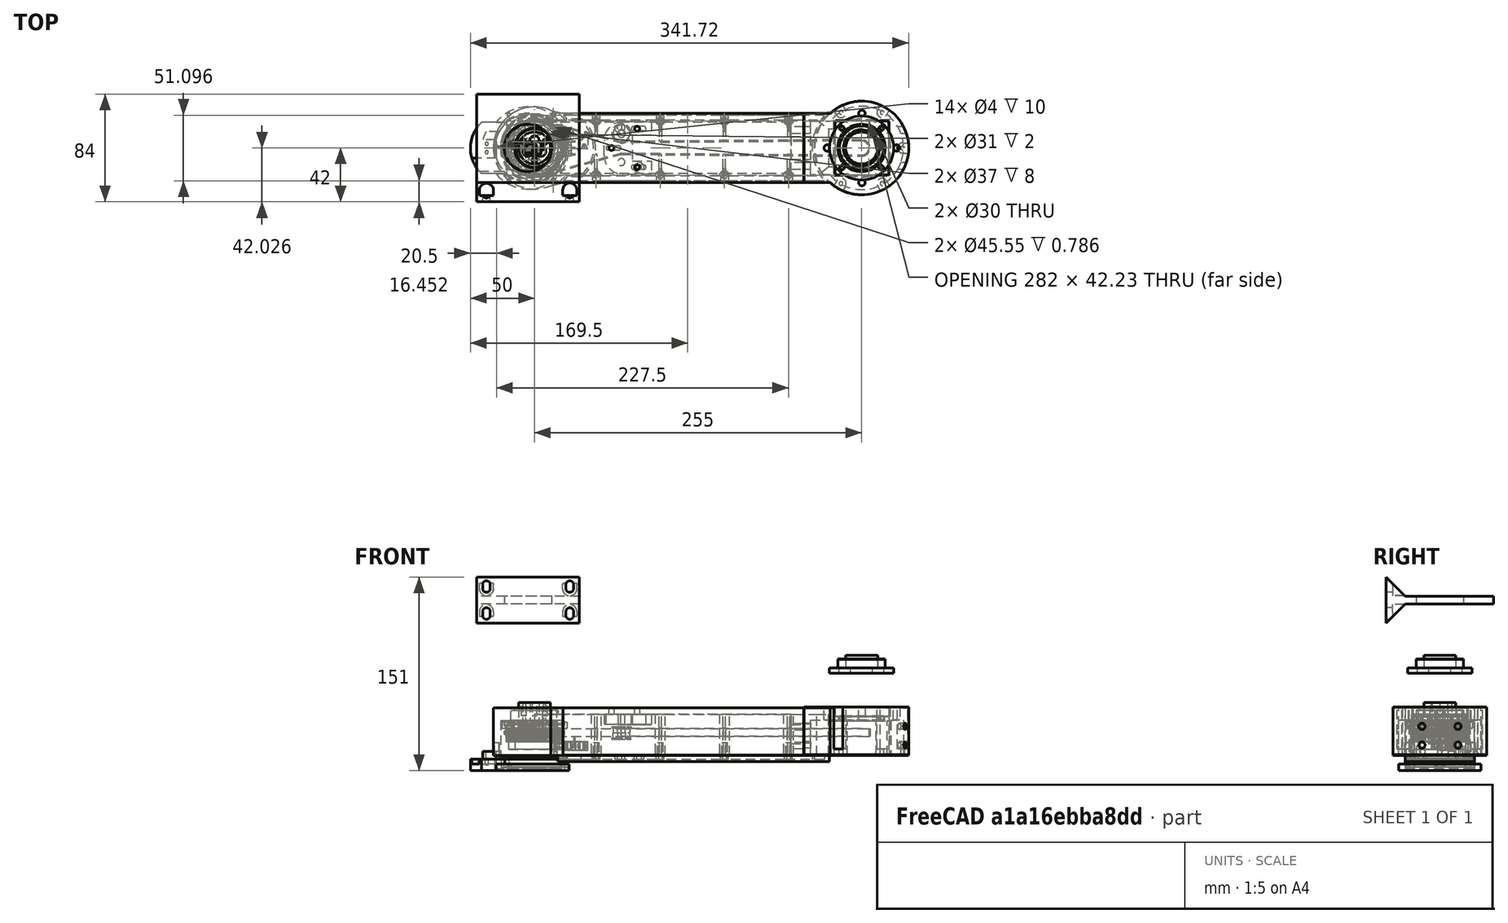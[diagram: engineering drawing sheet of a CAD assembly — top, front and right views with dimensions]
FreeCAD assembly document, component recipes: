
FREECAD ASSEMBLY — COMPONENT RECIPES ("GT2_80")

This assembly document has 18 components, labeled P0..P17 below (a component is one placed body or linked part). 13 of them carry a construction recipe — the FreeCAD feature program that regenerates the part from scratch, quoted from this document or its linked companion documents; the rest are supplied as boundary geometry only. No exploded tour is included for this assembly.
NOTE — this tour is split across 2 documents so each fits a 32k-token context. This is document 1: the component sections continue in the remaining 1 document, each repeating the header above.
COMPONENT P0 — recipe-attached ("Bearing6805-2RS", modeled in this document).
Construction recipe (the document's own serialized feature program — sketch geometry with constraints, then the solid features built on it; lengths are millimeters unless a unit is written):

FEATURE [Sketcher::SketchObject] Sketch032
  ArcFitTolerance = 0
  AttachmentSupport = -> [YZ_Plane007]
  FullyConstrained = false
  MakeInternals = false
  MapMode = 5
  Placement = pos=(0,0,0) rot=(0.57735,0.57735,0.57735;2.0944rad)
  expr: Constraints[16] = <<Spreadsheet>>.TopBearingHole / 2
  expr: Constraints[17] = <<Spreadsheet>>.TopBearingDiameter / 2
  sketch-geometry (12):
    g0: LineSegment StartX=12.5 StartY=3.5 StartZ=0 EndX=12.5 EndY=-3.5 EndZ=0
    g1: LineSegment StartX=12.5 StartY=3.5 StartZ=0 EndX=13.75 EndY=3.5 EndZ=0
    g2: LineSegment StartX=13.75 StartY=3.5 StartZ=0 EndX=14 EndY=3.25 EndZ=0
    g3: LineSegment StartX=14 StartY=3.25 StartZ=0 EndX=17.25 EndY=3.25 EndZ=0
    g4: LineSegment StartX=17.25 StartY=3.25 StartZ=0 EndX=17.5 EndY=3.5 EndZ=0
    g5: LineSegment StartX=17.5 StartY=3.5 StartZ=0 EndX=18.5 EndY=3.5 EndZ=0
    g6: LineSegment StartX=18.5 StartY=3.5 StartZ=0 EndX=18.5 EndY=-3.5 EndZ=0
    g7: LineSegment StartX=12.5 StartY=-3.5 StartZ=0 EndX=13.75 EndY=-3.5 EndZ=0
    g8: LineSegment StartX=13.75 StartY=-3.5 StartZ=0 EndX=14.6017 EndY=-3.46349 EndZ=0
    g9: LineSegment StartX=14.6017 StartY=-3.46349 StartZ=0 EndX=17.8517 EndY=-3.46349 EndZ=0
    g10: LineSegment StartX=17.8517 StartY=-3.46349 StartZ=0 EndX=17.5 EndY=-3.5 EndZ=0
    g11: LineSegment StartX=17.5 StartY=-3.5 StartZ=0 EndX=18.5 EndY=-3.5 EndZ=0
  constraints (34):
    c: Symmetric(g0,g0,g-1)
    c: DistanceY(g0,g0) = 7
    c: Coincident(g1,g0)
    c: Horizontal(g1)
    c: Coincident(g2,g1)
    c: Coincident(g3,g2)
    c: Horizontal(g3)
    c: Coincident(g4,g3)
    c: Coincident(g5,g4)
    c: Horizontal(g5)
    c: Coincident(g6,g5)
    c: Vertical(g6)
    c: Angle(g1,g2) = 2.35619
    c: DistanceY(g3,g5) = 0.25
    c: Horizontal(g4,g1)
    c: Equal(g4,g2)
    c: DistanceX(g-1,g0) = 12.5
    c: DistanceX(g-1,g6) = 18.5
    c: DistanceX(g1,g1) = 1.25
    c: DistanceX(g5,g5) = 1
    c: Equal(g0,g6)
    c: Coincident(g7,g0)
    c: Horizontal(g7)
    c: Equal(g1,g7)
    c: Coincident(g8,g7)
    c: Coincident(g9,g8)
    c: Horizontal(g9)
    c: Coincident(g10,g9)
    c: Coincident(g11,g10)
    c: Coincident(g11,g6)
    c: Horizontal(g11)
    c: Equal(g5,g11)
    c: Equal(g10,g4)
    c: Equal(g3,g9)
FEATURE [PartDesign::Revolution] Revolution
  Angle = 360
  Angle2 = 60
  Axis = (0,0,1)
  Base = (0,0,0)
  Placement = pos=(0,0,0) rot=(1,1,1;2.0944rad)
  Profile = -> Sketch032
  ReferenceAxis = -> Sketch032 [V_Axis]
  Reversed = true
  Suppressed = false
  Type = 0
FEATURE [PartDesign::Chamfer] Chamfer
  Angle = 45
  Base = -> Revolution [Edge11,Edge1,Edge10,Edge2]
  BaseFeature = -> Revolution
  ChamferType = 0
  FlipDirection = false
  Placement = pos=(0,0,0) rot=(1,1,1;2.0944rad)
  Size = 0.25
  Size2 = 1
  SupportTransform = false
  Suppressed = false
  UseAllEdges = false
FEATURE [PartDesign::Body] Body001  label="Bearing6805-2RS"
  AllowCompound = false
  Group = -> [Sketch032,Revolution,Chamfer]
  Origin = -> Origin007
  Placement = pos=(260,4e-16,56.4622) rot=(0,0,1;0rad)
  Tip = -> Chamfer
COMPONENT P1 — recipe-attached ("MainShaft", modeled in this document).
Construction recipe (the document's own serialized feature program — sketch geometry with constraints, then the solid features built on it; lengths are millimeters unless a unit is written):

FEATURE [Sketcher::SketchObject] Sketch
  ArcFitTolerance = 1e-06
  AttachmentSupport = -> [XZ_Plane008]
  FullyConstrained = true
  MakeInternals = false
  MapMode = 5
  Placement = pos=(0,0,0) rot=(1,0,0;1.5708rad)
  expr: Constraints[16] = <<Spreadsheet>>.TopBearingHole / 2
  expr: Constraints[17] = <<Spreadsheet>>.SecondShaftThroughHole / 2
  expr: Constraints[18] = <<Spreadsheet>>.TopThrustBearingDiameter / 2
  expr: Constraints[19] = <<Spreadsheet>>.TopThrustBearingDiameter / 2 + 2
  expr: Constraints[22] = <<Spreadsheet>>.TopThickness + <<Spreadsheet>>.TopBearingHeight + <<Spreadsheet>>.TopThrustBearingHeight + 5
  sketch-geometry (8):
    g0: LineSegment StartX=12.5 StartY=19 StartZ=0 EndX=12.5 EndY=1 EndZ=0
    g1: LineSegment StartX=12.5 StartY=1 StartZ=0 EndX=23.5 EndY=1 EndZ=0
    g2: LineSegment StartX=23.5 StartY=1 StartZ=0 EndX=23.5 EndY=4 EndZ=0
    g3: LineSegment StartX=23.5 StartY=4 StartZ=0 EndX=25.5 EndY=4 EndZ=0
    g4: LineSegment StartX=25.5 StartY=4 StartZ=0 EndX=25.5 EndY=-1 EndZ=0
    g5: LineSegment StartX=25.5 StartY=-1 StartZ=0 EndX=4 EndY=-1 EndZ=0
    g6: LineSegment StartX=4 StartY=-1 StartZ=0 EndX=4 EndY=19 EndZ=0
    g7: LineSegment StartX=4 StartY=19 StartZ=0 EndX=12.5 EndY=19 EndZ=0
  constraints (24):
    c: Coincident(g0,g1)
    c: Horizontal(g1)
    c: Coincident(g1,g2)
    c: Vertical(g2)
    c: Coincident(g2,g3)
    c: Horizontal(g3)
    c: Coincident(g3,g4)
    c: Vertical(g4)
    c: Coincident(g4,g5)
    c: Horizontal(g5)
    c: Coincident(g5,g6)
    c: Vertical(g6)
    c: Coincident(g6,g7)
    c: Coincident(g7,g0)
    c: Horizontal(g7)
    c: Vertical(g0,g0)
    c: Distance(g-2,g0) = 12.5
    c: Distance(g-2,g6) = 4
    c: Distance(g-2,g2) = 23.5
    c: Distance(g-2,g4) = 25.5
    c: Distance(g-1,g1) = 1
    c: Distance(g2,g2) = 3
    c: Distance(g-1,g7) = 19
    c: Distance(g-1,g5) = 1
FEATURE [PartDesign::Revolution] Revolution001
  Angle = 360
  Angle2 = 60
  Axis = (0,2e-16,1)
  Base = (0,0,0)
  Midplane = true
  Placement = pos=(0,0,0) rot=(1,0,0;1.5708rad)
  Profile = -> Sketch
  ReferenceAxis = -> Sketch [V_Axis]
  Refine = true
  Suppressed = false
  Type = 0
FEATURE [Sketcher::SketchObject] SketchGear
  ArcFitTolerance = 1e-06
  AttachmentSupport = -> [Revolution001]
  FullyConstrained = false
  MakeInternals = false
  MapMode = 5
  Placement = pos=(0,-2e-16,-1) rot=(1,0,0;3.14159rad)
  expr: Constraints[0] = <<Spreadsheet>>.SecondShaftThroughHole
  sketch-geometry (421):
    g0: ArcOfCircle CenterX=21.8777 CenterY=-0.75 CenterZ=0 NormalX=0 NormalY=0 NormalZ=1 AngleXU=7e-16 Radius=0.15 StartAngle=0 EndAngle=1.5708
    g1: ArcOfCircle CenterX=22.2237 CenterY=0.82798 CenterZ=0 NormalX=0 NormalY=0 NormalZ=-1 AngleXU=-1.3331 Radius=1.46929 StartAngle=0 EndAngle=0.255762
    g2: ArcOfCircle CenterX=21.8371 CenterY=0 CenterZ=0 NormalX=0 NormalY=0 NormalZ=-1 AngleXU=-0.984764 Radius=0.559359 StartAngle=0 EndAngle=1.96953
    g3: ArcOfCircle CenterX=22.2237 CenterY=-0.82798 CenterZ=0 NormalX=0 NormalY=0 NormalZ=-1 AngleXU=1.07734 Radius=1.46929 StartAngle=0 EndAngle=0.255762
    g4: ArcOfCircle CenterX=21.8777 CenterY=0.75 CenterZ=0 NormalX=0 NormalY=0 NormalZ=1 AngleXU=-1.5708 Radius=0.15 StartAngle=0 EndAngle=1.5708
    g5: LineSegment StartX=22.0277 StartY=0.75 StartZ=0 EndX=22.0062 EndY=1.22757 EndZ=0
    g6: ArcOfCircle CenterX=21.8568 CenterY=1.21412 CenterZ=0 NormalX=0 NormalY=0 NormalZ=1 AngleXU=0.0897598 Radius=0.15 StartAngle=0 EndAngle=1.5708
    g7: ArcOfCircle CenterX=22.06 CenterY=2.81676 CenterZ=0 NormalX=0 NormalY=0 NormalZ=-1 AngleXU=-1.42286 Radius=1.46929 StartAngle=0 EndAngle=0.255762
    g8: ArcOfCircle CenterX=21.7491 CenterY=1.95746 CenterZ=0 NormalX=0 NormalY=0 NormalZ=-1 AngleXU=-1.07452 Radius=0.559359 StartAngle=0 EndAngle=1.96953
    g9: ArcOfCircle CenterX=22.2084 CenterY=1.16747 CenterZ=0 NormalX=0 NormalY=0 NormalZ=-1 AngleXU=0.987578 Radius=1.46929 StartAngle=0 EndAngle=0.255762
    g10: ArcOfCircle CenterX=21.7224 CenterY=2.70808 CenterZ=0 NormalX=0 NormalY=0 NormalZ=1 AngleXU=-1.48104 Radius=0.15 StartAngle=0 EndAngle=1.5708
    g11: LineSegment StartX=21.8718 StartY=2.72153 StartZ=0 EndX=21.8076 EndY=3.19525 EndZ=0
    g12: ArcOfCircle CenterX=21.66 CenterY=3.16847 CenterZ=0 NormalX=0 NormalY=0 NormalZ=1 AngleXU=0.17952 Radius=0.15 StartAngle=0 EndAngle=1.5708
    g13: ArcOfCircle CenterX=21.7187 CenterY=4.78286 CenterZ=0 NormalX=0 NormalY=0 NormalZ=-1 AngleXU=-1.51262 Radius=1.46929 StartAngle=0 EndAngle=0.255762
    g14: ArcOfCircle CenterX=21.4861 CenterY=3.89916 CenterZ=0 NormalX=0 NormalY=0 NormalZ=-1 AngleXU=-1.16428 Radius=0.559359 StartAngle=0 EndAngle=1.96953
    g15: ArcOfCircle CenterX=22.0144 CenterY=3.15351 CenterZ=0 NormalX=0 NormalY=0 NormalZ=-1 AngleXU=0.897818 Radius=1.46929 StartAngle=0 EndAngle=0.255762
    g16: ArcOfCircle CenterX=21.3922 CenterY=4.64436 CenterZ=0 NormalX=0 NormalY=0 NormalZ=1 AngleXU=-1.39128 Radius=0.15 StartAngle=0 EndAngle=1.5708
    g17: LineSegment StartX=21.5398 StartY=4.67114 StartZ=0 EndX=21.4334 EndY=5.13721 EndZ=0
    g18: ArcOfCircle CenterX=21.2888 CenterY=5.0973 CenterZ=0 NormalX=0 NormalY=0 NormalZ=1 AngleXU=0.269279 Radius=0.15 StartAngle=0 EndAngle=1.5708
    g19: ArcOfCircle CenterX=21.2025 CenterY=6.71045 CenterZ=0 NormalX=0 NormalY=0 NormalZ=-1 AngleXU=-1.60238 Radius=1.46929 StartAngle=0 EndAngle=0.255762
    g20: ArcOfCircle CenterX=21.0501 CenterY=5.80946 CenterZ=0 NormalX=0 NormalY=0 NormalZ=-1 AngleXU=-1.25404 Radius=0.559359 StartAngle=0 EndAngle=1.96953
    g21: ArcOfCircle CenterX=21.6431 CenterY=5.11417 CenterZ=0 NormalX=0 NormalY=0 NormalZ=-1 AngleXU=0.808058 Radius=1.46929 StartAngle=0 EndAngle=0.255762
    g22: ArcOfCircle CenterX=20.8898 CenterY=6.54324 CenterZ=0 NormalX=0 NormalY=0 NormalZ=1 AngleXU=-1.30152 Radius=0.15 StartAngle=0 EndAngle=1.5708
    g23: LineSegment StartX=21.0343 StartY=6.58315 StartZ=0 EndX=20.8866 EndY=7.0378 EndZ=0
    g24: ArcOfCircle CenterX=20.7462 CenterY=6.98509 CenterZ=0 NormalX=0 NormalY=0 NormalZ=1 AngleXU=0.359039 Radius=0.15 StartAngle=0 EndAngle=1.5708
    g25: ArcOfCircle CenterX=20.5156 CenterY=8.58402 CenterZ=0 NormalX=0 NormalY=0 NormalZ=-1 AngleXU=-1.69214 Radius=1.46929 StartAngle=0 EndAngle=0.255762
    g26: ArcOfCircle CenterX=20.4446 CenterY=7.67299 CenterZ=0 NormalX=0 NormalY=0 NormalZ=-1 AngleXU=-1.3438 Radius=0.559359 StartAngle=0 EndAngle=1.96953
    g27: ArcOfCircle CenterX=21.0975 CenterY=7.03365 CenterZ=0 NormalX=0 NormalY=0 NormalZ=-1 AngleXU=0.718298 Radius=1.46929 StartAngle=0 EndAngle=0.255762
    g28: ArcOfCircle CenterX=20.2191 CenterY=8.38945 CenterZ=0 NormalX=0 NormalY=0 NormalZ=1 AngleXU=-1.21176 Radius=0.15 StartAngle=0 EndAngle=1.5708
    g29: LineSegment StartX=20.3596 StartY=8.44215 StartZ=0 EndX=20.1717 EndY=8.88173 EndZ=0
    g30: ArcOfCircle CenterX=20.0365 CenterY=8.81665 CenterZ=0 NormalX=0 NormalY=0 NormalZ=1 AngleXU=0.448799 Radius=0.15 StartAngle=0 EndAngle=1.5708
    g31: ArcOfCircle CenterX=19.6636 CenterY=10.3885 CenterZ=0 NormalX=0 NormalY=0 NormalZ=-1 AngleXU=-1.7819 Radius=1.46929 StartAngle=0 EndAngle=0.255762
    g32: ArcOfCircle CenterX=19.6745 CenterY=9.47474 CenterZ=0 NormalX=0 NormalY=0 NormalZ=-1 AngleXU=-1.43356 Radius=0.559359 StartAngle=0 EndAngle=1.96953
    g33: ArcOfCircle CenterX=20.3821 CenterY=8.8965 CenterZ=0 NormalX=0 NormalY=0 NormalZ=-1 AngleXU=0.628539 Radius=1.46929 StartAngle=0 EndAngle=0.255762
    g34: ArcOfCircle CenterX=19.3857 CenterY=10.1681 CenterZ=0 NormalX=0 NormalY=0 NormalZ=1 AngleXU=-1.122 Radius=0.15 StartAngle=0 EndAngle=1.5708
    g35: LineSegment StartX=19.5209 StartY=10.2332 StartZ=0 EndX=19.2943 EndY=10.6542 EndZ=0
    g36: ArcOfCircle CenterX=19.1656 CenterY=10.5772 CenterZ=0 NormalX=0 NormalY=0 NormalZ=1 AngleXU=0.538559 Radius=0.15 StartAngle=0 EndAngle=1.5708
    g37: ArcOfCircle CenterX=18.6532 CenterY=12.1093 CenterZ=0 NormalX=0 NormalY=0 NormalZ=-1 AngleXU=-1.87166 Radius=1.46929 StartAngle=0 EndAngle=0.255762
    g38: ArcOfCircle CenterX=18.746 CenterY=11.2002 CenterZ=0 NormalX=0 NormalY=0 NormalZ=-1 AngleXU=-1.52332 Radius=0.559359 StartAngle=0 EndAngle=1.96953
    g39: ArcOfCircle CenterX=19.5025 CenterY=10.6877 CenterZ=0 NormalX=0 NormalY=0 NormalZ=-1 AngleXU=0.538779 Radius=1.46929 StartAngle=0 EndAngle=0.255762
    g40: ArcOfCircle CenterX=18.3962 CenterY=11.8649 CenterZ=0 NormalX=0 NormalY=0 NormalZ=1 AngleXU=-1.03224 Radius=0.15 StartAngle=0 EndAngle=1.5708
    g41: LineSegment StartX=18.525 StartY=11.9418 StartZ=0 EndX=18.2616 EndY=12.3408 EndZ=0
    g42: ArcOfCircle CenterX=18.1403 CenterY=12.2526 CenterZ=0 NormalX=0 NormalY=0 NormalZ=1 AngleXU=0.628319 Radius=0.15 StartAngle=0 EndAngle=1.5708
    g43: ArcOfCircle CenterX=17.4926 CenterY=13.7326 CenterZ=0 NormalX=0 NormalY=0 NormalZ=-1 AngleXU=-1.96142 Radius=1.46929 StartAngle=0 EndAngle=0.255762
    g44: ArcOfCircle CenterX=17.6665 CenterY=12.8355 CenterZ=0 NormalX=0 NormalY=0 NormalZ=-1 AngleXU=-1.61308 Radius=0.559359 StartAngle=0 EndAngle=1.96953
    g45: ArcOfCircle CenterX=18.466 CenterY=12.3929 CenterZ=0 NormalX=0 NormalY=0 NormalZ=-1 AngleXU=0.449019 Radius=1.46929 StartAngle=0 EndAngle=0.255762
    g46: ArcOfCircle CenterX=17.2586 CenterY=13.4661 CenterZ=0 NormalX=0 NormalY=0 NormalZ=1 AngleXU=-0.942478 Radius=0.15 StartAngle=0 EndAngle=1.5708
    g47: LineSegment StartX=17.3799 StartY=13.5543 StartZ=0 EndX=17.0819 EndY=13.9281 EndZ=0
    g48: ArcOfCircle CenterX=16.9689 CenterY=13.8294 CenterZ=0 NormalX=0 NormalY=0 NormalZ=1 AngleXU=0.718078 Radius=0.15 StartAngle=0 EndAngle=1.5708
    g49: ArcOfCircle CenterX=16.1912 CenterY=15.2453 CenterZ=0 NormalX=0 NormalY=0 NormalZ=-1 AngleXU=-2.05118 Radius=1.46929 StartAngle=0 EndAngle=0.255762
    g50: ArcOfCircle CenterX=16.4449 CenterY=14.3674 CenterZ=0 NormalX=0 NormalY=0 NormalZ=-1 AngleXU=-1.70284 Radius=0.559359 StartAngle=0 EndAngle=1.96953
    g51: ArcOfCircle CenterX=17.2808 CenterY=13.9983 CenterZ=0 NormalX=0 NormalY=0 NormalZ=-1 AngleXU=0.359259 Radius=1.46929 StartAngle=0 EndAngle=0.255762
    g52: ArcOfCircle CenterX=15.982 CenterY=14.959 CenterZ=0 NormalX=0 NormalY=0 NormalZ=1 AngleXU=-0.852718 Radius=0.15 StartAngle=0 EndAngle=1.5708
    g53: LineSegment StartX=16.095 StartY=15.0577 StartZ=0 EndX=15.7646 EndY=15.4032 EndZ=0
    g54: ArcOfCircle CenterX=15.661 CenterY=15.2948 CenterZ=0 NormalX=0 NormalY=0 NormalZ=1 AngleXU=0.807838 Radius=0.15 StartAngle=0 EndAngle=1.5708
    g55: ArcOfCircle CenterX=14.7595 CenterY=16.6353 CenterZ=0 NormalX=0 NormalY=0 NormalZ=-1 AngleXU=-2.14094 Radius=1.46929 StartAngle=0 EndAngle=0.255762
    g56: ArcOfCircle CenterX=15.0908 CenterY=15.7837 CenterZ=0 NormalX=0 NormalY=0 NormalZ=-1 AngleXU=-1.7926 Radius=0.559359 StartAngle=0 EndAngle=1.96953
    g57: ArcOfCircle CenterX=15.9564 CenterY=15.491 CenterZ=0 NormalX=0 NormalY=0 NormalZ=-1 AngleXU=0.269499 Radius=1.46929 StartAngle=0 EndAngle=0.255762
    g58: ArcOfCircle CenterX=14.5768 CenterY=16.3314 CenterZ=0 NormalX=0 NormalY=0 NormalZ=1 AngleXU=-0.762958 Radius=0.15 StartAngle=0 EndAngle=1.5708
    g59: LineSegment StartX=14.6804 StartY=16.4398 StartZ=0 EndX=14.3204 EndY=16.7543 EndZ=0
    g60: ArcOfCircle CenterX=14.2269 CenterY=16.6371 CenterZ=0 NormalX=0 NormalY=0 NormalZ=1 AngleXU=0.897598 Radius=0.15 StartAngle=0 EndAngle=1.5708
    g61: ArcOfCircle CenterX=13.2089 CenterY=17.8914 CenterZ=0 NormalX=0 NormalY=0 NormalZ=-1 AngleXU=-2.2307 Radius=1.46929 StartAngle=0 EndAngle=0.255762
    g62: ArcOfCircle CenterX=13.6152 CenterY=17.0729 CenterZ=0 NormalX=0 NormalY=0 NormalZ=-1 AngleXU=-1.88236 Radius=0.559359 StartAngle=0 EndAngle=1.96953
    g63: ArcOfCircle CenterX=14.5036 CenterY=16.8589 CenterZ=0 NormalX=0 NormalY=0 NormalZ=-1 AngleXU=0.17974 Radius=1.46929 StartAngle=0 EndAngle=0.255762
    g64: ArcOfCircle CenterX=13.0541 CenterY=17.5723 CenterZ=0 NormalX=0 NormalY=0 NormalZ=1 AngleXU=-0.673198 Radius=0.15 StartAngle=0 EndAngle=1.5708
    g65: LineSegment StartX=13.1477 StartY=17.6896 StartZ=0 EndX=12.7609 EndY=17.9705 EndZ=0
    g66: ArcOfCircle CenterX=12.6783 CenterY=17.8454 CenterZ=0 NormalX=0 NormalY=0 NormalZ=1 AngleXU=0.987358 Radius=0.15 StartAngle=0 EndAngle=1.5708
    g67: ArcOfCircle CenterX=11.5519 CenterY=19.0034 CenterZ=0 NormalX=0 NormalY=0 NormalZ=-1 AngleXU=-2.32046 Radius=1.46929 StartAngle=0 EndAngle=0.255762
    g68: ArcOfCircle CenterX=12.03 CenterY=18.2246 CenterZ=0 NormalX=0 NormalY=0 NormalZ=-1 AngleXU=-1.97212 Radius=0.559359 StartAngle=0 EndAngle=1.96953
    g69: ArcOfCircle CenterX=12.934 CenterY=18.0911 CenterZ=0 NormalX=0 NormalY=0 NormalZ=-1 AngleXU=0.0899798 Radius=1.46929 StartAngle=0 EndAngle=0.255762
    g70: ArcOfCircle CenterX=11.4264 CenterY=18.6717 CenterZ=0 NormalX=0 NormalY=0 NormalZ=1 AngleXU=-0.583439 Radius=0.15 StartAngle=0 EndAngle=1.5708
    g71: LineSegment StartX=11.5091 StartY=18.7969 StartZ=0 EndX=11.0987 EndY=19.0421 EndZ=0
    g72: ArcOfCircle CenterX=11.0276 CenterY=18.91 CenterZ=0 NormalX=0 NormalY=0 NormalZ=1 AngleXU=1.07712 Radius=0.15 StartAngle=0 EndAngle=1.5708
    g73: ArcOfCircle CenterX=9.80198 CenterY=19.9624 CenterZ=0 NormalX=0 NormalY=0 NormalZ=-1 AngleXU=-2.41022 Radius=1.46929 StartAngle=0 EndAngle=0.255762
    g74: ArcOfCircle CenterX=10.3479 CenterY=19.2296 CenterZ=0 NormalX=0 NormalY=0 NormalZ=-1 AngleXU=-2.06188 Radius=0.559359 StartAngle=0 EndAngle=1.96953
    g75: ArcOfCircle CenterX=11.2602 CenterY=19.1777 CenterZ=0 NormalX=0 NormalY=0 NormalZ=-1 AngleXU=0.000220002 Radius=1.46929 StartAngle=0 EndAngle=0.255762
    g76: ArcOfCircle CenterX=9.70671 CenterY=19.6208 CenterZ=0 NormalX=0 NormalY=0 NormalZ=1 AngleXU=-0.493679 Radius=0.15 StartAngle=0 EndAngle=1.5708
    g77: LineSegment StartX=9.77779 StartY=19.7529 StartZ=0 EndX=9.34708 EndY=19.9603 EndZ=0
    g78: ArcOfCircle CenterX=9.28813 CenterY=19.8224 CenterZ=0 NormalX=0 NormalY=0 NormalZ=1 AngleXU=1.16688 Radius=0.15 StartAngle=0 EndAngle=1.5708
    g79: ArcOfCircle CenterX=7.9731 CenterY=20.7607 CenterZ=0 NormalX=0 NormalY=0 NormalZ=-1 AngleXU=-2.49998 Radius=1.46929 StartAngle=0 EndAngle=0.255762
    g80: ArcOfCircle CenterX=8.58251 CenterY=20.0798 CenterZ=0 NormalX=0 NormalY=0 NormalZ=-1 AngleXU=-2.15164 Radius=0.559359 StartAngle=0 EndAngle=1.96953
    g81: ArcOfCircle CenterX=9.49581 CenterY=20.1099 CenterZ=0 NormalX=0 NormalY=0 NormalZ=-1 AngleXU=-0.0895398 Radius=1.46929 StartAngle=0 EndAngle=0.255762
    g82: ArcOfCircle CenterX=7.90883 CenterY=20.4119 CenterZ=0 NormalX=0 NormalY=0 NormalZ=1 AngleXU=-0.403919 Radius=0.15 StartAngle=0 EndAngle=1.5708
    g83: LineSegment StartX=7.96779 StartY=20.5498 StartZ=0 EndX=7.52022 EndY=20.7178 EndZ=0
    g84: ArcOfCircle CenterX=7.47387 CenterY=20.5752 CenterZ=0 NormalX=0 NormalY=0 NormalZ=1 AngleXU=1.25664 Radius=0.15 StartAngle=0 EndAngle=1.5708
    g85: ArcOfCircle CenterX=6.08003 CenterY=21.3918 CenterZ=0 NormalX=0 NormalY=0 NormalZ=-1 AngleXU=-2.58974 Radius=1.46929 StartAngle=0 EndAngle=0.255762
    g86: ArcOfCircle CenterX=6.74802 CenterY=20.7683 CenterZ=0 NormalX=0 NormalY=0 NormalZ=-1 AngleXU=-2.2414 Radius=0.559359 StartAngle=0 EndAngle=1.96953
    g87: ArcOfCircle CenterX=7.65494 CenterY=20.8801 CenterZ=0 NormalX=0 NormalY=0 NormalZ=-1 AngleXU=-0.1793 Radius=1.46929 StartAngle=0 EndAngle=0.255762
    g88: ArcOfCircle CenterX=6.04729 CenterY=21.0387 CenterZ=0 NormalX=0 NormalY=0 NormalZ=1 AngleXU=-0.314159 Radius=0.15 StartAngle=0 EndAngle=1.5708
    g89: LineSegment StartX=6.09364 StartY=21.1813 StartZ=0 EndX=5.63282 EndY=21.3085 EndZ=0
    g90: ArcOfCircle CenterX=5.59944 CenterY=21.1623 CenterZ=0 NormalX=0 NormalY=0 NormalZ=1 AngleXU=1.3464 Radius=0.15 StartAngle=0 EndAngle=1.5708
    g91: ArcOfCircle CenterX=4.13801 CenterY=21.8507 CenterZ=0 NormalX=0 NormalY=0 NormalZ=-1 AngleXU=-2.6795 Radius=1.46929 StartAngle=0 EndAngle=0.255762
    g92: ArcOfCircle CenterX=4.8592 CenterY=21.2896 CenterZ=0 NormalX=0 NormalY=0 NormalZ=-1 AngleXU=-2.33116 Radius=0.559359 StartAngle=0 EndAngle=1.96953
    g93: ArcOfCircle CenterX=5.75245 CenterY=21.4822 CenterZ=0 NormalX=0 NormalY=0 NormalZ=-1 AngleXU=-0.269059 Radius=1.46929 StartAngle=0 EndAngle=0.255762
    g94: ArcOfCircle CenterX=4.13705 CenterY=21.4961 CenterZ=0 NormalX=0 NormalY=0 NormalZ=1 AngleXU=-0.224399 Radius=0.15 StartAngle=0 EndAngle=1.5708
    g95: LineSegment StartX=4.17043 StartY=21.6423 StartZ=0 EndX=3.70006 EndY=21.7277 EndZ=0
    g96: ArcOfCircle CenterX=3.67993 CenterY=21.579 CenterZ=0 NormalX=0 NormalY=0 NormalZ=1 AngleXU=1.43616 Radius=0.15 StartAngle=0 EndAngle=1.5708
    g97: ArcOfCircle CenterX=2.16267 CenterY=22.1337 CenterZ=0 NormalX=0 NormalY=0 NormalZ=-1 AngleXU=-2.76926 Radius=1.46929 StartAngle=0 EndAngle=0.255762
    g98: ArcOfCircle CenterX=2.93126 CenterY=21.6394 CenterZ=0 NormalX=0 NormalY=0 NormalZ=-1 AngleXU=-2.42092 Radius=0.559359 StartAngle=0 EndAngle=1.96953
    g99: ArcOfCircle CenterX=3.80364 CenterY=21.9114 CenterZ=0 NormalX=0 NormalY=0 NormalZ=-1 AngleXU=-0.358819 Radius=1.46929 StartAngle=0 EndAngle=0.255762
    g100: ArcOfCircle CenterX=2.1935 CenterY=21.7804 CenterZ=0 NormalX=0 NormalY=0 NormalZ=1 AngleXU=-0.13464 Radius=0.15 StartAngle=0 EndAngle=1.5708
    g101: LineSegment StartX=2.21364 StartY=21.929 StartZ=0 EndX=1.73751 EndY=21.9719 EndZ=0
    g102: ArcOfCircle CenterX=1.73078 CenterY=21.822 CenterZ=0 NormalX=0 NormalY=0 NormalZ=1 AngleXU=1.52592 Radius=0.15 StartAngle=0 EndAngle=1.5708
    g103: ArcOfCircle CenterX=0.169914 CenterY=22.2384 CenterZ=0 NormalX=0 NormalY=0 NormalZ=-1 AngleXU=-2.85902 Radius=1.46929 StartAngle=0 EndAngle=0.255762
    g104: ArcOfCircle CenterX=0.979716 CenterY=21.8151 CenterZ=0 NormalX=0 NormalY=0 NormalZ=-1 AngleXU=-2.51068 Radius=0.559359 StartAngle=0 EndAngle=1.96953
    g105: ArcOfCircle CenterX=1.82421 CenterY=22.1641 CenterZ=0 NormalX=0 NormalY=0 NormalZ=-1 AngleXU=-0.448579 Radius=1.46929 StartAngle=0 EndAngle=0.255762
    g106: ArcOfCircle CenterX=0.232294 CenterY=21.8893 CenterZ=0 NormalX=0 NormalY=0 NormalZ=1 AngleXU=-0.0448799 Radius=0.15 StartAngle=0 EndAngle=1.5708
    g107: LineSegment StartX=0.239024 StartY=22.0392 StartZ=0 EndX=-0.239024 EndY=22.0392 EndZ=0
    g108: ArcOfCircle CenterX=-0.232294 CenterY=21.8893 CenterZ=0 NormalX=0 NormalY=0 NormalZ=1 AngleXU=1.61568 Radius=0.15 StartAngle=0 EndAngle=1.5708
    g109: ArcOfCircle CenterX=-1.82421 CenterY=22.1641 CenterZ=0 NormalX=0 NormalY=0 NormalZ=-1 AngleXU=-2.94878 Radius=1.46929 StartAngle=0 EndAngle=0.255762
    g110: ArcOfCircle CenterX=-0.979716 CenterY=21.8151 CenterZ=0 NormalX=0 NormalY=0 NormalZ=-1 AngleXU=-2.60044 Radius=0.559359 StartAngle=0 EndAngle=1.96953
    g111: ArcOfCircle CenterX=-0.169914 CenterY=22.2384 CenterZ=0 NormalX=0 NormalY=0 NormalZ=-1 AngleXU=-0.538339 Radius=1.46929 StartAngle=0 EndAngle=0.255762
    g112: ArcOfCircle CenterX=-1.73078 CenterY=21.822 CenterZ=0 NormalX=0 NormalY=0 NormalZ=1 AngleXU=0.0448799 Radius=0.15 StartAngle=0 EndAngle=1.5708
    g113: LineSegment StartX=-1.73751 StartY=21.9719 StartZ=0 EndX=-2.21364 EndY=21.929 EndZ=0
    g114: ArcOfCircle CenterX=-2.1935 CenterY=21.7804 CenterZ=0 NormalX=0 NormalY=0 NormalZ=1 AngleXU=1.70544 Radius=0.15 StartAngle=0 EndAngle=1.5708
    g115: ArcOfCircle CenterX=-3.80364 CenterY=21.9114 CenterZ=0 NormalX=0 NormalY=0 NormalZ=-1 AngleXU=-3.03854 Radius=1.46929 StartAngle=0 EndAngle=0.255762
    g116: ArcOfCircle CenterX=-2.93126 CenterY=21.6394 CenterZ=0 NormalX=0 NormalY=0 NormalZ=-1 AngleXU=-2.6902 Radius=0.559359 StartAngle=0 EndAngle=1.96953
    g117: ArcOfCircle CenterX=-2.16267 CenterY=22.1337 CenterZ=0 NormalX=0 NormalY=0 NormalZ=-1 AngleXU=-0.628099 Radius=1.46929 StartAngle=0 EndAngle=0.255762
    g118: ArcOfCircle CenterX=-3.67993 CenterY=21.579 CenterZ=0 NormalX=0 NormalY=0 NormalZ=1 AngleXU=0.13464 Radius=0.15 StartAngle=0 EndAngle=1.5708
    g119: LineSegment StartX=-3.70006 StartY=21.7277 StartZ=0 EndX=-4.17043 EndY=21.6423 EndZ=0
    g120: ArcOfCircle CenterX=-4.13705 CenterY=21.4961 CenterZ=0 NormalX=0 NormalY=0 NormalZ=1 AngleXU=1.7952 Radius=0.15 StartAngle=0 EndAngle=1.5708
    g121: ArcOfCircle CenterX=-5.75245 CenterY=21.4822 CenterZ=0 NormalX=0 NormalY=0 NormalZ=-1 AngleXU=-3.1283 Radius=1.46929 StartAngle=0 EndAngle=0.255762
    g122: ArcOfCircle CenterX=-4.8592 CenterY=21.2896 CenterZ=0 NormalX=0 NormalY=0 NormalZ=-1 AngleXU=-2.77996 Radius=0.559359 StartAngle=0 EndAngle=1.96953
    g123: ArcOfCircle CenterX=-4.13801 CenterY=21.8507 CenterZ=0 NormalX=0 NormalY=0 NormalZ=-1 AngleXU=-0.717858 Radius=1.46929 StartAngle=0 EndAngle=0.255762
    g124: ArcOfCircle CenterX=-5.59944 CenterY=21.1623 CenterZ=0 NormalX=0 NormalY=0 NormalZ=1 AngleXU=0.224399 Radius=0.15 StartAngle=0 EndAngle=1.5708
    g125: LineSegment StartX=-5.63282 StartY=21.3085 StartZ=0 EndX=-6.09364 EndY=21.1813 EndZ=0
    g126: ArcOfCircle CenterX=-6.04729 CenterY=21.0387 CenterZ=0 NormalX=0 NormalY=0 NormalZ=1 AngleXU=1.88496 Radius=0.15 StartAngle=0 EndAngle=1.5708
    g127: ArcOfCircle CenterX=-7.65494 CenterY=20.8801 CenterZ=0 NormalX=0 NormalY=0 NormalZ=-1 AngleXU=3.06513 Radius=1.46929 StartAngle=0 EndAngle=0.255762
    g128: ArcOfCircle CenterX=-6.74802 CenterY=20.7683 CenterZ=0 NormalX=0 NormalY=0 NormalZ=-1 AngleXU=-2.86972 Radius=0.559359 StartAngle=0 EndAngle=1.96953
    g129: ArcOfCircle CenterX=-6.08003 CenterY=21.3918 CenterZ=0 NormalX=0 NormalY=0 NormalZ=-1 AngleXU=-0.807618 Radius=1.46929 StartAngle=0 EndAngle=0.255762
    g130: ArcOfCircle CenterX=-7.47387 CenterY=20.5752 CenterZ=0 NormalX=0 NormalY=0 NormalZ=1 AngleXU=0.314159 Radius=0.15 StartAngle=0 EndAngle=1.5708
    g131: LineSegment StartX=-7.52022 StartY=20.7178 StartZ=0 EndX=-7.96779 EndY=20.5498 EndZ=0
    g132: ArcOfCircle CenterX=-7.90883 CenterY=20.4119 CenterZ=0 NormalX=0 NormalY=0 NormalZ=1 AngleXU=1.97472 Radius=0.15 StartAngle=0 EndAngle=1.5708
    g133: ArcOfCircle CenterX=-9.49581 CenterY=20.1099 CenterZ=0 NormalX=0 NormalY=0 NormalZ=-1 AngleXU=2.97537 Radius=1.46929 StartAngle=0 EndAngle=0.255762
    g134: ArcOfCircle CenterX=-8.58251 CenterY=20.0798 CenterZ=0 NormalX=0 NormalY=0 NormalZ=-1 AngleXU=-2.95948 Radius=0.559359 StartAngle=0 EndAngle=1.96953
    g135: ArcOfCircle CenterX=-7.9731 CenterY=20.7607 CenterZ=0 NormalX=0 NormalY=0 NormalZ=-1 AngleXU=-0.897378 Radius=1.46929 StartAngle=0 EndAngle=0.255762
    g136: ArcOfCircle CenterX=-9.28813 CenterY=19.8224 CenterZ=0 NormalX=0 NormalY=0 NormalZ=1 AngleXU=0.403919 Radius=0.15 StartAngle=0 EndAngle=1.5708
    g137: LineSegment StartX=-9.34708 StartY=19.9603 StartZ=0 EndX=-9.77779 EndY=19.7529 EndZ=0
    g138: ArcOfCircle CenterX=-9.70671 CenterY=19.6208 CenterZ=0 NormalX=0 NormalY=0 NormalZ=1 AngleXU=2.06448 Radius=0.15 StartAngle=0 EndAngle=1.5708
    g139: ArcOfCircle CenterX=-11.2602 CenterY=19.1777 CenterZ=0 NormalX=0 NormalY=0 NormalZ=-1 AngleXU=2.88561 Radius=1.46929 StartAngle=0 EndAngle=0.255762
    g140: ArcOfCircle CenterX=-10.3479 CenterY=19.2296 CenterZ=0 NormalX=0 NormalY=0 NormalZ=-1 AngleXU=-3.04924 Radius=0.559359 StartAngle=0 EndAngle=1.96953
    g141: ArcOfCircle CenterX=-9.80198 CenterY=19.9624 CenterZ=0 NormalX=0 NormalY=0 NormalZ=-1 AngleXU=-0.987138 Radius=1.46929 StartAngle=0 EndAngle=0.255762
    g142: ArcOfCircle CenterX=-11.0276 CenterY=18.91 CenterZ=0 NormalX=0 NormalY=0 NormalZ=1 AngleXU=0.493679 Radius=0.15 StartAngle=0 EndAngle=1.5708
    g143: LineSegment StartX=-11.0987 StartY=19.0421 StartZ=0 EndX=-11.5091 EndY=18.7969 EndZ=0
    g144: ArcOfCircle CenterX=-11.4264 CenterY=18.6717 CenterZ=0 NormalX=0 NormalY=0 NormalZ=1 AngleXU=2.15423 Radius=0.15 StartAngle=0 EndAngle=1.5708
    g145: ArcOfCircle CenterX=-12.934 CenterY=18.0911 CenterZ=0 NormalX=0 NormalY=0 NormalZ=-1 AngleXU=2.79585 Radius=1.46929 StartAngle=0 EndAngle=0.255762
    g146: ArcOfCircle CenterX=-12.03 CenterY=18.2246 CenterZ=0 NormalX=0 NormalY=0 NormalZ=-1 AngleXU=-3.139 Radius=0.559359 StartAngle=0 EndAngle=1.96953
    g147: ArcOfCircle CenterX=-11.5519 CenterY=19.0034 CenterZ=0 NormalX=0 NormalY=0 NormalZ=-1 AngleXU=-1.0769 Radius=1.46929 StartAngle=0 EndAngle=0.255762
    g148: ArcOfCircle CenterX=-12.6783 CenterY=17.8454 CenterZ=0 NormalX=0 NormalY=0 NormalZ=1 AngleXU=0.583439 Radius=0.15 StartAngle=0 EndAngle=1.5708
    g149: LineSegment StartX=-12.7609 StartY=17.9705 StartZ=0 EndX=-13.1477 EndY=17.6896 EndZ=0
    g150: ArcOfCircle CenterX=-13.0541 CenterY=17.5723 CenterZ=0 NormalX=0 NormalY=0 NormalZ=1 AngleXU=2.24399 Radius=0.15 StartAngle=0 EndAngle=1.5708
    g151: ArcOfCircle CenterX=-14.5036 CenterY=16.8589 CenterZ=0 NormalX=0 NormalY=0 NormalZ=-1 AngleXU=2.70609 Radius=1.46929 StartAngle=0 EndAngle=0.255762
    g152: ArcOfCircle CenterX=-13.6152 CenterY=17.0729 CenterZ=0 NormalX=0 NormalY=0 NormalZ=-1 AngleXU=3.05443 Radius=0.559359 StartAngle=0 EndAngle=1.96953
    g153: ArcOfCircle CenterX=-13.2089 CenterY=17.8914 CenterZ=0 NormalX=0 NormalY=0 NormalZ=-1 AngleXU=-1.16666 Radius=1.46929 StartAngle=0 EndAngle=0.255762
    g154: ArcOfCircle CenterX=-14.2269 CenterY=16.6371 CenterZ=0 NormalX=0 NormalY=0 NormalZ=1 AngleXU=0.673198 Radius=0.15 StartAngle=0 EndAngle=1.5708
    g155: LineSegment StartX=-14.3204 StartY=16.7543 StartZ=0 EndX=-14.6804 EndY=16.4398 EndZ=0
    g156: ArcOfCircle CenterX=-14.5768 CenterY=16.3314 CenterZ=0 NormalX=0 NormalY=0 NormalZ=1 AngleXU=2.33375 Radius=0.15 StartAngle=0 EndAngle=1.5708
    g157: ArcOfCircle CenterX=-15.9564 CenterY=15.491 CenterZ=0 NormalX=0 NormalY=0 NormalZ=-1 AngleXU=2.61633 Radius=1.46929 StartAngle=0 EndAngle=0.255762
    g158: ArcOfCircle CenterX=-15.0908 CenterY=15.7837 CenterZ=0 NormalX=0 NormalY=0 NormalZ=-1 AngleXU=2.96467 Radius=0.559359 StartAngle=0 EndAngle=1.96953
    g159: ArcOfCircle CenterX=-14.7595 CenterY=16.6353 CenterZ=0 NormalX=0 NormalY=0 NormalZ=-1 AngleXU=-1.25642 Radius=1.46929 StartAngle=0 EndAngle=0.255762
    g160: ArcOfCircle CenterX=-15.661 CenterY=15.2948 CenterZ=0 NormalX=0 NormalY=0 NormalZ=1 AngleXU=0.762958 Radius=0.15 StartAngle=0 EndAngle=1.5708
    g161: LineSegment StartX=-15.7646 StartY=15.4032 StartZ=0 EndX=-16.095 EndY=15.0577 EndZ=0
    g162: ArcOfCircle CenterX=-15.982 CenterY=14.959 CenterZ=0 NormalX=0 NormalY=0 NormalZ=1 AngleXU=2.42351 Radius=0.15 StartAngle=0 EndAngle=1.5708
    g163: ArcOfCircle CenterX=-17.2808 CenterY=13.9983 CenterZ=0 NormalX=0 NormalY=0 NormalZ=-1 AngleXU=2.52657 Radius=1.46929 StartAngle=0 EndAngle=0.255762
    g164: ArcOfCircle CenterX=-16.4449 CenterY=14.3674 CenterZ=0 NormalX=0 NormalY=0 NormalZ=-1 AngleXU=2.87491 Radius=0.559359 StartAngle=0 EndAngle=1.96953
    g165: ArcOfCircle CenterX=-16.1912 CenterY=15.2453 CenterZ=0 NormalX=0 NormalY=0 NormalZ=-1 AngleXU=-1.34618 Radius=1.46929 StartAngle=0 EndAngle=0.255762
    g166: ArcOfCircle CenterX=-16.9689 CenterY=13.8294 CenterZ=0 NormalX=0 NormalY=0 NormalZ=1 AngleXU=0.852718 Radius=0.15 StartAngle=0 EndAngle=1.5708
    g167: LineSegment StartX=-17.0819 StartY=13.9281 StartZ=0 EndX=-17.3799 EndY=13.5543 EndZ=0
    g168: ArcOfCircle CenterX=-17.2586 CenterY=13.4661 CenterZ=0 NormalX=0 NormalY=0 NormalZ=1 AngleXU=2.51327 Radius=0.15 StartAngle=0 EndAngle=1.5708
    g169: ArcOfCircle CenterX=-18.466 CenterY=12.3929 CenterZ=0 NormalX=0 NormalY=0 NormalZ=-1 AngleXU=2.43681 Radius=1.46929 StartAngle=0 EndAngle=0.255762
    g170: ArcOfCircle CenterX=-17.6665 CenterY=12.8355 CenterZ=0 NormalX=0 NormalY=0 NormalZ=-1 AngleXU=2.78515 Radius=0.559359 StartAngle=0 EndAngle=1.96953
    g171: ArcOfCircle CenterX=-17.4926 CenterY=13.7326 CenterZ=0 NormalX=0 NormalY=0 NormalZ=-1 AngleXU=-1.43594 Radius=1.46929 StartAngle=0 EndAngle=0.255762
    g172: ArcOfCircle CenterX=-18.1403 CenterY=12.2526 CenterZ=0 NormalX=0 NormalY=0 NormalZ=1 AngleXU=0.942478 Radius=0.15 StartAngle=0 EndAngle=1.5708
    g173: LineSegment StartX=-18.2616 StartY=12.3408 StartZ=0 EndX=-18.525 EndY=11.9418 EndZ=0
    g174: ArcOfCircle CenterX=-18.3962 CenterY=11.8649 CenterZ=0 NormalX=0 NormalY=0 NormalZ=1 AngleXU=2.60303 Radius=0.15 StartAngle=0 EndAngle=1.5708
    g175: ArcOfCircle CenterX=-19.5025 CenterY=10.6877 CenterZ=0 NormalX=0 NormalY=0 NormalZ=-1 AngleXU=2.34705 Radius=1.46929 StartAngle=0 EndAngle=0.255762
    g176: ArcOfCircle CenterX=-18.746 CenterY=11.2002 CenterZ=0 NormalX=0 NormalY=0 NormalZ=-1 AngleXU=2.69539 Radius=0.559359 StartAngle=0 EndAngle=1.96953
    g177: ArcOfCircle CenterX=-18.6532 CenterY=12.1093 CenterZ=0 NormalX=0 NormalY=0 NormalZ=-1 AngleXU=-1.5257 Radius=1.46929 StartAngle=0 EndAngle=0.255762
    g178: ArcOfCircle CenterX=-19.1656 CenterY=10.5772 CenterZ=0 NormalX=0 NormalY=0 NormalZ=1 AngleXU=1.03224 Radius=0.15 StartAngle=0 EndAngle=1.5708
    g179: LineSegment StartX=-19.2943 StartY=10.6542 StartZ=0 EndX=-19.5209 EndY=10.2332 EndZ=0
    g180: ArcOfCircle CenterX=-19.3857 CenterY=10.1681 CenterZ=0 NormalX=0 NormalY=0 NormalZ=1 AngleXU=2.69279 Radius=0.15 StartAngle=0 EndAngle=1.5708
    g181: ArcOfCircle CenterX=-20.3821 CenterY=8.8965 CenterZ=0 NormalX=0 NormalY=0 NormalZ=-1 AngleXU=2.25729 Radius=1.46929 StartAngle=0 EndAngle=0.255762
    g182: ArcOfCircle CenterX=-19.6745 CenterY=9.47474 CenterZ=0 NormalX=0 NormalY=0 NormalZ=-1 AngleXU=2.60563 Radius=0.559359 StartAngle=0 EndAngle=1.96953
    g183: ArcOfCircle CenterX=-19.6636 CenterY=10.3885 CenterZ=0 NormalX=0 NormalY=0 NormalZ=-1 AngleXU=-1.61546 Radius=1.46929 StartAngle=0 EndAngle=0.255762
    g184: ArcOfCircle CenterX=-20.0365 CenterY=8.81665 CenterZ=0 NormalX=0 NormalY=0 NormalZ=1 AngleXU=1.122 Radius=0.15 StartAngle=0 EndAngle=1.5708
    g185: LineSegment StartX=-20.1717 StartY=8.88173 StartZ=0 EndX=-20.3596 EndY=8.44215 EndZ=0
    g186: ArcOfCircle CenterX=-20.2191 CenterY=8.38945 CenterZ=0 NormalX=0 NormalY=0 NormalZ=1 AngleXU=2.78255 Radius=0.15 StartAngle=0 EndAngle=1.5708
    g187: ArcOfCircle CenterX=-21.0975 CenterY=7.03365 CenterZ=0 NormalX=0 NormalY=0 NormalZ=-1 AngleXU=2.16753 Radius=1.46929 StartAngle=0 EndAngle=0.255762
    g188: ArcOfCircle CenterX=-20.4446 CenterY=7.67299 CenterZ=0 NormalX=0 NormalY=0 NormalZ=-1 AngleXU=2.51587 Radius=0.559359 StartAngle=0 EndAngle=1.96953
    g189: ArcOfCircle CenterX=-20.5156 CenterY=8.58402 CenterZ=0 NormalX=0 NormalY=0 NormalZ=-1 AngleXU=-1.70522 Radius=1.46929 StartAngle=0 EndAngle=0.255762
    g190: ArcOfCircle CenterX=-20.7462 CenterY=6.98509 CenterZ=0 NormalX=0 NormalY=0 NormalZ=1 AngleXU=1.21176 Radius=0.15 StartAngle=0 EndAngle=1.5708
    g191: LineSegment StartX=-20.8866 StartY=7.0378 StartZ=0 EndX=-21.0343 EndY=6.58315 EndZ=0
    g192: ArcOfCircle CenterX=-20.8898 CenterY=6.54324 CenterZ=0 NormalX=0 NormalY=0 NormalZ=1 AngleXU=2.87231 Radius=0.15 StartAngle=0 EndAngle=1.5708
    g193: ArcOfCircle CenterX=-21.6431 CenterY=5.11417 CenterZ=0 NormalX=0 NormalY=0 NormalZ=-1 AngleXU=2.07777 Radius=1.46929 StartAngle=0 EndAngle=0.255762
    g194: ArcOfCircle CenterX=-21.0501 CenterY=5.80946 CenterZ=0 NormalX=0 NormalY=0 NormalZ=-1 AngleXU=2.42611 Radius=0.559359 StartAngle=0 EndAngle=1.96953
    g195: ArcOfCircle CenterX=-21.2025 CenterY=6.71045 CenterZ=0 NormalX=0 NormalY=0 NormalZ=-1 AngleXU=-1.79498 Radius=1.46929 StartAngle=0 EndAngle=0.255762
    g196: ArcOfCircle CenterX=-21.2888 CenterY=5.0973 CenterZ=0 NormalX=0 NormalY=0 NormalZ=1 AngleXU=1.30152 Radius=0.15 StartAngle=0 EndAngle=1.5708
    g197: LineSegment StartX=-21.4334 StartY=5.13721 StartZ=0 EndX=-21.5398 EndY=4.67114 EndZ=0
    g198: ArcOfCircle CenterX=-21.3922 CenterY=4.64436 CenterZ=0 NormalX=0 NormalY=0 NormalZ=1 AngleXU=2.96207 Radius=0.15 StartAngle=0 EndAngle=1.5708
    g199: ArcOfCircle CenterX=-22.0144 CenterY=3.15351 CenterZ=0 NormalX=0 NormalY=0 NormalZ=-1 AngleXU=1.98801 Radius=1.46929 StartAngle=0 EndAngle=0.255762
    g200: ArcOfCircle CenterX=-21.4861 CenterY=3.89916 CenterZ=0 NormalX=0 NormalY=0 NormalZ=-1 AngleXU=2.33635 Radius=0.559359 StartAngle=0 EndAngle=1.96953
    g201: ArcOfCircle CenterX=-21.7187 CenterY=4.78286 CenterZ=0 NormalX=0 NormalY=0 NormalZ=-1 AngleXU=-1.88474 Radius=1.46929 StartAngle=0 EndAngle=0.255762
    g202: ArcOfCircle CenterX=-21.66 CenterY=3.16847 CenterZ=0 NormalX=0 NormalY=0 NormalZ=1 AngleXU=1.39128 Radius=0.15 StartAngle=0 EndAngle=1.5708
    g203: LineSegment StartX=-21.8076 StartY=3.19525 StartZ=0 EndX=-21.8718 EndY=2.72153 EndZ=0
    g204: ArcOfCircle CenterX=-21.7224 CenterY=2.70808 CenterZ=0 NormalX=0 NormalY=0 NormalZ=1 AngleXU=3.05183 Radius=0.15 StartAngle=0 EndAngle=1.5708
    g205: ArcOfCircle CenterX=-22.2084 CenterY=1.16747 CenterZ=0 NormalX=0 NormalY=0 NormalZ=-1 AngleXU=1.89825 Radius=1.46929 StartAngle=0 EndAngle=0.255762
    g206: ArcOfCircle CenterX=-21.7491 CenterY=1.95746 CenterZ=0 NormalX=0 NormalY=0 NormalZ=-1 AngleXU=2.24659 Radius=0.559359 StartAngle=0 EndAngle=1.96953
    g207: ArcOfCircle CenterX=-22.06 CenterY=2.81676 CenterZ=0 NormalX=0 NormalY=0 NormalZ=-1 AngleXU=-1.9745 Radius=1.46929 StartAngle=0 EndAngle=0.255762
    g208: ArcOfCircle CenterX=-21.8568 CenterY=1.21412 CenterZ=0 NormalX=0 NormalY=0 NormalZ=1 AngleXU=1.48104 Radius=0.15 StartAngle=0 EndAngle=1.5708
    g209: LineSegment StartX=-22.0062 StartY=1.22757 StartZ=0 EndX=-22.0277 EndY=0.75 EndZ=0
    g210: ArcOfCircle CenterX=-21.8777 CenterY=0.75 CenterZ=0 NormalX=0 NormalY=0 NormalZ=1 AngleXU=-3.14159 Radius=0.15 StartAngle=0 EndAngle=1.5708
    g211: ArcOfCircle CenterX=-22.2237 CenterY=-0.82798 CenterZ=0 NormalX=0 NormalY=0 NormalZ=-1 AngleXU=1.80849 Radius=1.46929 StartAngle=0 EndAngle=0.255762
    g212: ArcOfCircle CenterX=-21.8371 CenterY=3.6e-15 CenterZ=0 NormalX=0 NormalY=0 NormalZ=-1 AngleXU=2.15683 Radius=0.559359 StartAngle=0 EndAngle=1.96953
    g213: ArcOfCircle CenterX=-22.2237 CenterY=0.82798 CenterZ=0 NormalX=0 NormalY=0 NormalZ=-1 AngleXU=-2.06426 Radius=1.46929 StartAngle=0 EndAngle=0.255762
    g214: ArcOfCircle CenterX=-21.8777 CenterY=-0.75 CenterZ=0 NormalX=0 NormalY=0 NormalZ=1 AngleXU=1.5708 Radius=0.15 StartAngle=0 EndAngle=1.5708
    g215: LineSegment StartX=-22.0277 StartY=-0.75 StartZ=0 EndX=-22.0062 EndY=-1.22757 EndZ=0
    g216: ArcOfCircle CenterX=-21.8568 CenterY=-1.21412 CenterZ=0 NormalX=0 NormalY=0 NormalZ=1 AngleXU=-3.05183 Radius=0.15 StartAngle=0 EndAngle=1.5708
    g217: ArcOfCircle CenterX=-22.06 CenterY=-2.81676 CenterZ=0 NormalX=0 NormalY=0 NormalZ=-1 AngleXU=1.71873 Radius=1.46929 StartAngle=0 EndAngle=0.255762
    g218: ArcOfCircle CenterX=-21.7491 CenterY=-1.95746 CenterZ=0 NormalX=0 NormalY=0 NormalZ=-1 AngleXU=2.06707 Radius=0.559359 StartAngle=0 EndAngle=1.96953
    g219: ArcOfCircle CenterX=-22.2084 CenterY=-1.16747 CenterZ=0 NormalX=0 NormalY=0 NormalZ=-1 AngleXU=-2.15401 Radius=1.46929 StartAngle=0 EndAngle=0.255762
    g220: ArcOfCircle CenterX=-21.7224 CenterY=-2.70808 CenterZ=0 NormalX=0 NormalY=0 NormalZ=1 AngleXU=1.66056 Radius=0.15 StartAngle=0 EndAngle=1.5708
    g221: LineSegment StartX=-21.8718 StartY=-2.72153 StartZ=0 EndX=-21.8076 EndY=-3.19525 EndZ=0
    g222: ArcOfCircle CenterX=-21.66 CenterY=-3.16847 CenterZ=0 NormalX=0 NormalY=0 NormalZ=1 AngleXU=-2.96207 Radius=0.15 StartAngle=0 EndAngle=1.5708
    g223: ArcOfCircle CenterX=-21.7187 CenterY=-4.78286 CenterZ=0 NormalX=0 NormalY=0 NormalZ=-1 AngleXU=1.62897 Radius=1.46929 StartAngle=0 EndAngle=0.255762
    g224: ArcOfCircle CenterX=-21.4861 CenterY=-3.89916 CenterZ=0 NormalX=0 NormalY=0 NormalZ=-1 AngleXU=1.97731 Radius=0.559359 StartAngle=0 EndAngle=1.96953
    g225: ArcOfCircle CenterX=-22.0144 CenterY=-3.15351 CenterZ=0 NormalX=0 NormalY=0 NormalZ=-1 AngleXU=-2.24377 Radius=1.46929 StartAngle=0 EndAngle=0.255762
    g226: ArcOfCircle CenterX=-21.3922 CenterY=-4.64436 CenterZ=0 NormalX=0 NormalY=0 NormalZ=1 AngleXU=1.75032 Radius=0.15 StartAngle=0 EndAngle=1.5708
    g227: LineSegment StartX=-21.5398 StartY=-4.67114 StartZ=0 EndX=-21.4334 EndY=-5.13721 EndZ=0
    g228: ArcOfCircle CenterX=-21.2888 CenterY=-5.0973 CenterZ=0 NormalX=0 NormalY=0 NormalZ=1 AngleXU=-2.87231 Radius=0.15 StartAngle=0 EndAngle=1.5708
    g229: ArcOfCircle CenterX=-21.2025 CenterY=-6.71045 CenterZ=0 NormalX=0 NormalY=0 NormalZ=-1 AngleXU=1.53921 Radius=1.46929 StartAngle=0 EndAngle=0.255762
    g230: ArcOfCircle CenterX=-21.0501 CenterY=-5.80946 CenterZ=0 NormalX=0 NormalY=0 NormalZ=-1 AngleXU=1.88755 Radius=0.559359 StartAngle=0 EndAngle=1.96953
    g231: ArcOfCircle CenterX=-21.6431 CenterY=-5.11417 CenterZ=0 NormalX=0 NormalY=0 NormalZ=-1 AngleXU=-2.33353 Radius=1.46929 StartAngle=0 EndAngle=0.255762
    g232: ArcOfCircle CenterX=-20.8898 CenterY=-6.54324 CenterZ=0 NormalX=0 NormalY=0 NormalZ=1 AngleXU=1.84008 Radius=0.15 StartAngle=0 EndAngle=1.5708
    g233: LineSegment StartX=-21.0343 StartY=-6.58315 StartZ=0 EndX=-20.8866 EndY=-7.0378 EndZ=0
    g234: ArcOfCircle CenterX=-20.7462 CenterY=-6.98509 CenterZ=0 NormalX=0 NormalY=0 NormalZ=1 AngleXU=-2.78255 Radius=0.15 StartAngle=0 EndAngle=1.5708
    g235: ArcOfCircle CenterX=-20.5156 CenterY=-8.58402 CenterZ=0 NormalX=0 NormalY=0 NormalZ=-1 AngleXU=1.44945 Radius=1.46929 StartAngle=0 EndAngle=0.255762
    g236: ArcOfCircle CenterX=-20.4446 CenterY=-7.67299 CenterZ=0 NormalX=0 NormalY=0 NormalZ=-1 AngleXU=1.79779 Radius=0.559359 StartAngle=0 EndAngle=1.96953
    g237: ArcOfCircle CenterX=-21.0975 CenterY=-7.03365 CenterZ=0 NormalX=0 NormalY=0 NormalZ=-1 AngleXU=-2.42329 Radius=1.46929 StartAngle=0 EndAngle=0.255762
    g238: ArcOfCircle CenterX=-20.2191 CenterY=-8.38945 CenterZ=0 NormalX=0 NormalY=0 NormalZ=1 AngleXU=1.92984 Radius=0.15 StartAngle=0 EndAngle=1.5708
    g239: LineSegment StartX=-20.3596 StartY=-8.44215 StartZ=0 EndX=-20.1717 EndY=-8.88173 EndZ=0
    g240: ArcOfCircle CenterX=-20.0365 CenterY=-8.81665 CenterZ=0 NormalX=0 NormalY=0 NormalZ=1 AngleXU=-2.69279 Radius=0.15 StartAngle=0 EndAngle=1.5708
    g241: ArcOfCircle CenterX=-19.6636 CenterY=-10.3885 CenterZ=0 NormalX=0 NormalY=0 NormalZ=-1 AngleXU=1.35969 Radius=1.46929 StartAngle=0 EndAngle=0.255762
    g242: ArcOfCircle CenterX=-19.6745 CenterY=-9.47474 CenterZ=0 NormalX=0 NormalY=0 NormalZ=-1 AngleXU=1.70803 Radius=0.559359 StartAngle=0 EndAngle=1.96953
    g243: ArcOfCircle CenterX=-20.3821 CenterY=-8.8965 CenterZ=0 NormalX=0 NormalY=0 NormalZ=-1 AngleXU=-2.51305 Radius=1.46929 StartAngle=0 EndAngle=0.255762
    g244: ArcOfCircle CenterX=-19.3857 CenterY=-10.1681 CenterZ=0 NormalX=0 NormalY=0 NormalZ=1 AngleXU=2.0196 Radius=0.15 StartAngle=0 EndAngle=1.5708
    g245: LineSegment StartX=-19.5209 StartY=-10.2332 StartZ=0 EndX=-19.2943 EndY=-10.6542 EndZ=0
    g246: ArcOfCircle CenterX=-19.1656 CenterY=-10.5772 CenterZ=0 NormalX=0 NormalY=0 NormalZ=1 AngleXU=-2.60303 Radius=0.15 StartAngle=0 EndAngle=1.5708
    g247: ArcOfCircle CenterX=-18.6532 CenterY=-12.1093 CenterZ=0 NormalX=0 NormalY=0 NormalZ=-1 AngleXU=1.26993 Radius=1.46929 StartAngle=0 EndAngle=0.255762
    g248: ArcOfCircle CenterX=-18.746 CenterY=-11.2002 CenterZ=0 NormalX=0 NormalY=0 NormalZ=-1 AngleXU=1.61827 Radius=0.559359 StartAngle=0 EndAngle=1.96953
    g249: ArcOfCircle CenterX=-19.5025 CenterY=-10.6877 CenterZ=0 NormalX=0 NormalY=0 NormalZ=-1 AngleXU=-2.60281 Radius=1.46929 StartAngle=0 EndAngle=0.255762
    g250: ArcOfCircle CenterX=-18.3962 CenterY=-11.8649 CenterZ=0 NormalX=0 NormalY=0 NormalZ=1 AngleXU=2.10936 Radius=0.15 StartAngle=0 EndAngle=1.5708
    g251: LineSegment StartX=-18.525 StartY=-11.9418 StartZ=0 EndX=-18.2616 EndY=-12.3408 EndZ=0
    g252: ArcOfCircle CenterX=-18.1403 CenterY=-12.2526 CenterZ=0 NormalX=0 NormalY=0 NormalZ=1 AngleXU=-2.51327 Radius=0.15 StartAngle=0 EndAngle=1.5708
    g253: ArcOfCircle CenterX=-17.4926 CenterY=-13.7326 CenterZ=0 NormalX=0 NormalY=0 NormalZ=-1 AngleXU=1.18017 Radius=1.46929 StartAngle=0 EndAngle=0.255762
    g254: ArcOfCircle CenterX=-17.6665 CenterY=-12.8355 CenterZ=0 NormalX=0 NormalY=0 NormalZ=-1 AngleXU=1.52851 Radius=0.559359 StartAngle=0 EndAngle=1.96953
    g255: ArcOfCircle CenterX=-18.466 CenterY=-12.3929 CenterZ=0 NormalX=0 NormalY=0 NormalZ=-1 AngleXU=-2.69257 Radius=1.46929 StartAngle=0 EndAngle=0.255762
    g256: ArcOfCircle CenterX=-17.2586 CenterY=-13.4661 CenterZ=0 NormalX=0 NormalY=0 NormalZ=1 AngleXU=2.19911 Radius=0.15 StartAngle=0 EndAngle=1.5708
    g257: LineSegment StartX=-17.3799 StartY=-13.5543 StartZ=0 EndX=-17.0819 EndY=-13.9281 EndZ=0
    g258: ArcOfCircle CenterX=-16.9689 CenterY=-13.8294 CenterZ=0 NormalX=0 NormalY=0 NormalZ=1 AngleXU=-2.42351 Radius=0.15 StartAngle=0 EndAngle=1.5708
    g259: ArcOfCircle CenterX=-16.1912 CenterY=-15.2453 CenterZ=0 NormalX=0 NormalY=0 NormalZ=-1 AngleXU=1.09042 Radius=1.46929 StartAngle=0 EndAngle=0.255762
    g260: ArcOfCircle CenterX=-16.4449 CenterY=-14.3674 CenterZ=0 NormalX=0 NormalY=0 NormalZ=-1 AngleXU=1.43875 Radius=0.559359 StartAngle=0 EndAngle=1.96953
    g261: ArcOfCircle CenterX=-17.2808 CenterY=-13.9983 CenterZ=0 NormalX=0 NormalY=0 NormalZ=-1 AngleXU=-2.78233 Radius=1.46929 StartAngle=0 EndAngle=0.255762
    g262: ArcOfCircle CenterX=-15.982 CenterY=-14.959 CenterZ=0 NormalX=0 NormalY=0 NormalZ=1 AngleXU=2.28887 Radius=0.15 StartAngle=0 EndAngle=1.5708
    g263: LineSegment StartX=-16.095 StartY=-15.0577 StartZ=0 EndX=-15.7646 EndY=-15.4032 EndZ=0
    g264: ArcOfCircle CenterX=-15.661 CenterY=-15.2948 CenterZ=0 NormalX=0 NormalY=0 NormalZ=1 AngleXU=-2.33375 Radius=0.15 StartAngle=0 EndAngle=1.5708
    g265: ArcOfCircle CenterX=-14.7595 CenterY=-16.6353 CenterZ=0 NormalX=0 NormalY=0 NormalZ=-1 AngleXU=1.00066 Radius=1.46929 StartAngle=0 EndAngle=0.255762
    g266: ArcOfCircle CenterX=-15.0908 CenterY=-15.7837 CenterZ=0 NormalX=0 NormalY=0 NormalZ=-1 AngleXU=1.34899 Radius=0.559359 StartAngle=0 EndAngle=1.96953
    g267: ArcOfCircle CenterX=-15.9564 CenterY=-15.491 CenterZ=0 NormalX=0 NormalY=0 NormalZ=-1 AngleXU=-2.87209 Radius=1.46929 StartAngle=0 EndAngle=0.255762
    g268: ArcOfCircle CenterX=-14.5768 CenterY=-16.3314 CenterZ=0 NormalX=0 NormalY=0 NormalZ=1 AngleXU=2.37863 Radius=0.15 StartAngle=0 EndAngle=1.5708
    g269: LineSegment StartX=-14.6804 StartY=-16.4398 StartZ=0 EndX=-14.3204 EndY=-16.7543 EndZ=0
    g270: ArcOfCircle CenterX=-14.2269 CenterY=-16.6371 CenterZ=0 NormalX=0 NormalY=0 NormalZ=1 AngleXU=-2.24399 Radius=0.15 StartAngle=0 EndAngle=1.5708
    g271: ArcOfCircle CenterX=-13.2089 CenterY=-17.8914 CenterZ=0 NormalX=0 NormalY=0 NormalZ=-1 AngleXU=0.910896 Radius=1.46929 StartAngle=0 EndAngle=0.255762
    g272: ArcOfCircle CenterX=-13.6152 CenterY=-17.0729 CenterZ=0 NormalX=0 NormalY=0 NormalZ=-1 AngleXU=1.25923 Radius=0.559359 StartAngle=0 EndAngle=1.96953
    g273: ArcOfCircle CenterX=-14.5036 CenterY=-16.8589 CenterZ=0 NormalX=0 NormalY=0 NormalZ=-1 AngleXU=-2.96185 Radius=1.46929 StartAngle=0 EndAngle=0.255762
    g274: ArcOfCircle CenterX=-13.0541 CenterY=-17.5723 CenterZ=0 NormalX=0 NormalY=0 NormalZ=1 AngleXU=2.46839 Radius=0.15 StartAngle=0 EndAngle=1.5708
    g275: LineSegment StartX=-13.1477 StartY=-17.6896 StartZ=0 EndX=-12.7609 EndY=-17.9705 EndZ=0
    g276: ArcOfCircle CenterX=-12.6783 CenterY=-17.8454 CenterZ=0 NormalX=0 NormalY=0 NormalZ=1 AngleXU=-2.15423 Radius=0.15 StartAngle=0 EndAngle=1.5708
    g277: ArcOfCircle CenterX=-11.5519 CenterY=-19.0034 CenterZ=0 NormalX=0 NormalY=0 NormalZ=-1 AngleXU=0.821136 Radius=1.46929 StartAngle=0 EndAngle=0.255762
    g278: ArcOfCircle CenterX=-12.03 CenterY=-18.2246 CenterZ=0 NormalX=0 NormalY=0 NormalZ=-1 AngleXU=1.16947 Radius=0.559359 StartAngle=0 EndAngle=1.96953
    g279: ArcOfCircle CenterX=-12.934 CenterY=-18.0911 CenterZ=0 NormalX=0 NormalY=0 NormalZ=-1 AngleXU=-3.05161 Radius=1.46929 StartAngle=0 EndAngle=0.255762
    g280: ArcOfCircle CenterX=-11.4264 CenterY=-18.6717 CenterZ=0 NormalX=0 NormalY=0 NormalZ=1 AngleXU=2.55815 Radius=0.15 StartAngle=0 EndAngle=1.5708
    g281: LineSegment StartX=-11.5091 StartY=-18.7969 StartZ=0 EndX=-11.0987 EndY=-19.0421 EndZ=0
    g282: ArcOfCircle CenterX=-11.0276 CenterY=-18.91 CenterZ=0 NormalX=0 NormalY=0 NormalZ=1 AngleXU=-2.06448 Radius=0.15 StartAngle=0 EndAngle=1.5708
    g283: ArcOfCircle CenterX=-9.80198 CenterY=-19.9624 CenterZ=0 NormalX=0 NormalY=0 NormalZ=-1 AngleXU=0.731376 Radius=1.46929 StartAngle=0 EndAngle=0.255762
    g284: ArcOfCircle CenterX=-10.3479 CenterY=-19.2296 CenterZ=0 NormalX=0 NormalY=0 NormalZ=-1 AngleXU=1.07971 Radius=0.559359 StartAngle=0 EndAngle=1.96953
    g285: ArcOfCircle CenterX=-11.2602 CenterY=-19.1777 CenterZ=0 NormalX=0 NormalY=0 NormalZ=-1 AngleXU=-3.14137 Radius=1.46929 StartAngle=0 EndAngle=0.255762
    g286: ArcOfCircle CenterX=-9.70671 CenterY=-19.6208 CenterZ=0 NormalX=0 NormalY=0 NormalZ=1 AngleXU=2.64791 Radius=0.15 StartAngle=0 EndAngle=1.5708
    g287: LineSegment StartX=-9.77779 StartY=-19.7529 StartZ=0 EndX=-9.34708 EndY=-19.9603 EndZ=0
    g288: ArcOfCircle CenterX=-9.28813 CenterY=-19.8224 CenterZ=0 NormalX=0 NormalY=0 NormalZ=1 AngleXU=-1.97472 Radius=0.15 StartAngle=0 EndAngle=1.5708
    g289: ArcOfCircle CenterX=-7.9731 CenterY=-20.7607 CenterZ=0 NormalX=0 NormalY=0 NormalZ=-1 AngleXU=0.641616 Radius=1.46929 StartAngle=0 EndAngle=0.255762
    g290: ArcOfCircle CenterX=-8.58251 CenterY=-20.0798 CenterZ=0 NormalX=0 NormalY=0 NormalZ=-1 AngleXU=0.989952 Radius=0.559359 StartAngle=0 EndAngle=1.96953
    g291: ArcOfCircle CenterX=-9.49581 CenterY=-20.1099 CenterZ=0 NormalX=0 NormalY=0 NormalZ=-1 AngleXU=3.05205 Radius=1.46929 StartAngle=0 EndAngle=0.255762
    g292: ArcOfCircle CenterX=-7.90883 CenterY=-20.4119 CenterZ=0 NormalX=0 NormalY=0 NormalZ=1 AngleXU=2.73767 Radius=0.15 StartAngle=0 EndAngle=1.5708
    g293: LineSegment StartX=-7.96779 StartY=-20.5498 StartZ=0 EndX=-7.52022 EndY=-20.7178 EndZ=0
    g294: ArcOfCircle CenterX=-7.47387 CenterY=-20.5752 CenterZ=0 NormalX=0 NormalY=0 NormalZ=1 AngleXU=-1.88496 Radius=0.15 StartAngle=0 EndAngle=1.5708
    g295: ArcOfCircle CenterX=-6.08003 CenterY=-21.3918 CenterZ=0 NormalX=0 NormalY=0 NormalZ=-1 AngleXU=0.551856 Radius=1.46929 StartAngle=0 EndAngle=0.255762
    g296: ArcOfCircle CenterX=-6.74802 CenterY=-20.7683 CenterZ=0 NormalX=0 NormalY=0 NormalZ=-1 AngleXU=0.900192 Radius=0.559359 StartAngle=0 EndAngle=1.96953
    g297: ArcOfCircle CenterX=-7.65494 CenterY=-20.8801 CenterZ=0 NormalX=0 NormalY=0 NormalZ=-1 AngleXU=2.96229 Radius=1.46929 StartAngle=0 EndAngle=0.255762
    g298: ArcOfCircle CenterX=-6.04729 CenterY=-21.0387 CenterZ=0 NormalX=0 NormalY=0 NormalZ=1 AngleXU=2.82743 Radius=0.15 StartAngle=0 EndAngle=1.5708
    g299: LineSegment StartX=-6.09364 StartY=-21.1813 StartZ=0 EndX=-5.63282 EndY=-21.3085 EndZ=0
    g300: ArcOfCircle CenterX=-5.59944 CenterY=-21.1623 CenterZ=0 NormalX=0 NormalY=0 NormalZ=1 AngleXU=-1.7952 Radius=0.15 StartAngle=0 EndAngle=1.5708
    g301: ArcOfCircle CenterX=-4.13801 CenterY=-21.8507 CenterZ=0 NormalX=0 NormalY=0 NormalZ=-1 AngleXU=0.462097 Radius=1.46929 StartAngle=0 EndAngle=0.255762
    g302: ArcOfCircle CenterX=-4.8592 CenterY=-21.2896 CenterZ=0 NormalX=0 NormalY=0 NormalZ=-1 AngleXU=0.810432 Radius=0.559359 StartAngle=0 EndAngle=1.96953
    g303: ArcOfCircle CenterX=-5.75245 CenterY=-21.4822 CenterZ=0 NormalX=0 NormalY=0 NormalZ=-1 AngleXU=2.87253 Radius=1.46929 StartAngle=0 EndAngle=0.255762
    g304: ArcOfCircle CenterX=-4.13705 CenterY=-21.4961 CenterZ=0 NormalX=0 NormalY=0 NormalZ=1 AngleXU=2.91719 Radius=0.15 StartAngle=0 EndAngle=1.5708
    g305: LineSegment StartX=-4.17043 StartY=-21.6423 StartZ=0 EndX=-3.70006 EndY=-21.7277 EndZ=0
    g306: ArcOfCircle CenterX=-3.67993 CenterY=-21.579 CenterZ=0 NormalX=0 NormalY=0 NormalZ=1 AngleXU=-1.70544 Radius=0.15 StartAngle=0 EndAngle=1.5708
    g307: ArcOfCircle CenterX=-2.16267 CenterY=-22.1337 CenterZ=0 NormalX=0 NormalY=0 NormalZ=-1 AngleXU=0.372337 Radius=1.46929 StartAngle=0 EndAngle=0.255762
    g308: ArcOfCircle CenterX=-2.93126 CenterY=-21.6394 CenterZ=0 NormalX=0 NormalY=0 NormalZ=-1 AngleXU=0.720672 Radius=0.559359 StartAngle=0 EndAngle=1.96953
    g309: ArcOfCircle CenterX=-3.80364 CenterY=-21.9114 CenterZ=0 NormalX=0 NormalY=0 NormalZ=-1 AngleXU=2.78277 Radius=1.46929 StartAngle=0 EndAngle=0.255762
    g310: ArcOfCircle CenterX=-2.1935 CenterY=-21.7804 CenterZ=0 NormalX=0 NormalY=0 NormalZ=1 AngleXU=3.00695 Radius=0.15 StartAngle=0 EndAngle=1.5708
    g311: LineSegment StartX=-2.21364 StartY=-21.929 StartZ=0 EndX=-1.73751 EndY=-21.9719 EndZ=0
    g312: ArcOfCircle CenterX=-1.73078 CenterY=-21.822 CenterZ=0 NormalX=0 NormalY=0 NormalZ=1 AngleXU=-1.61568 Radius=0.15 StartAngle=0 EndAngle=1.5708
    g313: ArcOfCircle CenterX=-0.169914 CenterY=-22.2384 CenterZ=0 NormalX=0 NormalY=0 NormalZ=-1 AngleXU=0.282577 Radius=1.46929 StartAngle=0 EndAngle=0.255762
    g314: ArcOfCircle CenterX=-0.979716 CenterY=-21.8151 CenterZ=0 NormalX=0 NormalY=0 NormalZ=-1 AngleXU=0.630913 Radius=0.559359 StartAngle=0 EndAngle=1.96953
    g315: ArcOfCircle CenterX=-1.82421 CenterY=-22.1641 CenterZ=0 NormalX=0 NormalY=0 NormalZ=-1 AngleXU=2.69301 Radius=1.46929 StartAngle=0 EndAngle=0.255762
    g316: ArcOfCircle CenterX=-0.232294 CenterY=-21.8893 CenterZ=0 NormalX=0 NormalY=0 NormalZ=1 AngleXU=3.09671 Radius=0.15 StartAngle=0 EndAngle=1.5708
    g317: LineSegment StartX=-0.239024 StartY=-22.0392 StartZ=0 EndX=0.239024 EndY=-22.0392 EndZ=0
    g318: ArcOfCircle CenterX=0.232294 CenterY=-21.8893 CenterZ=0 NormalX=0 NormalY=0 NormalZ=1 AngleXU=-1.52592 Radius=0.15 StartAngle=0 EndAngle=1.5708
    g319: ArcOfCircle CenterX=1.82421 CenterY=-22.1641 CenterZ=0 NormalX=0 NormalY=0 NormalZ=-1 AngleXU=0.192817 Radius=1.46929 StartAngle=0 EndAngle=0.255762
    g320: ArcOfCircle CenterX=0.979716 CenterY=-21.8151 CenterZ=0 NormalX=0 NormalY=0 NormalZ=-1 AngleXU=0.541153 Radius=0.559359 StartAngle=0 EndAngle=1.96953
    g321: ArcOfCircle CenterX=0.169914 CenterY=-22.2384 CenterZ=0 NormalX=0 NormalY=0 NormalZ=-1 AngleXU=2.60325 Radius=1.46929 StartAngle=0 EndAngle=0.255762
    g322: ArcOfCircle CenterX=1.73078 CenterY=-21.822 CenterZ=0 NormalX=0 NormalY=0 NormalZ=1 AngleXU=-3.09671 Radius=0.15 StartAngle=0 EndAngle=1.5708
    g323: LineSegment StartX=1.73751 StartY=-21.9719 StartZ=0 EndX=2.21364 EndY=-21.929 EndZ=0
    g324: ArcOfCircle CenterX=2.1935 CenterY=-21.7804 CenterZ=0 NormalX=0 NormalY=0 NormalZ=1 AngleXU=-1.43616 Radius=0.15 StartAngle=0 EndAngle=1.5708
    g325: ArcOfCircle CenterX=3.80364 CenterY=-21.9114 CenterZ=0 NormalX=0 NormalY=0 NormalZ=-1 AngleXU=0.103057 Radius=1.46929 StartAngle=0 EndAngle=0.255762
    g326: ArcOfCircle CenterX=2.93126 CenterY=-21.6394 CenterZ=0 NormalX=0 NormalY=0 NormalZ=-1 AngleXU=0.451393 Radius=0.559359 StartAngle=0 EndAngle=1.96953
    g327: ArcOfCircle CenterX=2.16267 CenterY=-22.1337 CenterZ=0 NormalX=0 NormalY=0 NormalZ=-1 AngleXU=2.51349 Radius=1.46929 StartAngle=0 EndAngle=0.255762
    g328: ArcOfCircle CenterX=3.67993 CenterY=-21.579 CenterZ=0 NormalX=0 NormalY=0 NormalZ=1 AngleXU=-3.00695 Radius=0.15 StartAngle=0 EndAngle=1.5708
    g329: LineSegment StartX=3.70006 StartY=-21.7277 StartZ=0 EndX=4.17043 EndY=-21.6423 EndZ=0
    g330: ArcOfCircle CenterX=4.13705 CenterY=-21.4961 CenterZ=0 NormalX=0 NormalY=0 NormalZ=1 AngleXU=-1.3464 Radius=0.15 StartAngle=0 EndAngle=1.5708
    g331: ArcOfCircle CenterX=5.75245 CenterY=-21.4822 CenterZ=0 NormalX=0 NormalY=0 NormalZ=-1 AngleXU=0.0132976 Radius=1.46929 StartAngle=0 EndAngle=0.255762
    g332: ArcOfCircle CenterX=4.8592 CenterY=-21.2896 CenterZ=0 NormalX=0 NormalY=0 NormalZ=-1 AngleXU=0.361633 Radius=0.559359 StartAngle=0 EndAngle=1.96953
    g333: ArcOfCircle CenterX=4.13801 CenterY=-21.8507 CenterZ=0 NormalX=0 NormalY=0 NormalZ=-1 AngleXU=2.42373 Radius=1.46929 StartAngle=0 EndAngle=0.255762
    g334: ArcOfCircle CenterX=5.59944 CenterY=-21.1623 CenterZ=0 NormalX=0 NormalY=0 NormalZ=1 AngleXU=-2.91719 Radius=0.15 StartAngle=0 EndAngle=1.5708
    g335: LineSegment StartX=5.63282 StartY=-21.3085 StartZ=0 EndX=6.09364 EndY=-21.1813 EndZ=0
    g336: ArcOfCircle CenterX=6.04729 CenterY=-21.0387 CenterZ=0 NormalX=0 NormalY=0 NormalZ=1 AngleXU=-1.25664 Radius=0.15 StartAngle=0 EndAngle=1.5708
    g337: ArcOfCircle CenterX=7.65494 CenterY=-20.8801 CenterZ=0 NormalX=0 NormalY=0 NormalZ=-1 AngleXU=-0.0764622 Radius=1.46929 StartAngle=0 EndAngle=0.255762
    g338: ArcOfCircle CenterX=6.74802 CenterY=-20.7683 CenterZ=0 NormalX=0 NormalY=0 NormalZ=-1 AngleXU=0.271874 Radius=0.559359 StartAngle=0 EndAngle=1.96953
    g339: ArcOfCircle CenterX=6.08003 CenterY=-21.3918 CenterZ=0 NormalX=0 NormalY=0 NormalZ=-1 AngleXU=2.33397 Radius=1.46929 StartAngle=0 EndAngle=0.255762
    g340: ArcOfCircle CenterX=7.47387 CenterY=-20.5752 CenterZ=0 NormalX=0 NormalY=0 NormalZ=1 AngleXU=-2.82743 Radius=0.15 StartAngle=0 EndAngle=1.5708
    g341: LineSegment StartX=7.52022 StartY=-20.7178 StartZ=0 EndX=7.96779 EndY=-20.5498 EndZ=0
    g342: ArcOfCircle CenterX=7.90883 CenterY=-20.4119 CenterZ=0 NormalX=0 NormalY=0 NormalZ=1 AngleXU=-1.16688 Radius=0.15 StartAngle=0 EndAngle=1.5708
    g343: ArcOfCircle CenterX=9.49581 CenterY=-20.1099 CenterZ=0 NormalX=0 NormalY=0 NormalZ=-1 AngleXU=-0.166222 Radius=1.46929 StartAngle=0 EndAngle=0.255762
    g344: ArcOfCircle CenterX=8.58251 CenterY=-20.0798 CenterZ=0 NormalX=0 NormalY=0 NormalZ=-1 AngleXU=0.182114 Radius=0.559359 StartAngle=0 EndAngle=1.96953
    g345: ArcOfCircle CenterX=7.9731 CenterY=-20.7607 CenterZ=0 NormalX=0 NormalY=0 NormalZ=-1 AngleXU=2.24421 Radius=1.46929 StartAngle=0 EndAngle=0.255762
    g346: ArcOfCircle CenterX=9.28813 CenterY=-19.8224 CenterZ=0 NormalX=0 NormalY=0 NormalZ=1 AngleXU=-2.73767 Radius=0.15 StartAngle=0 EndAngle=1.5708
    g347: LineSegment StartX=9.34708 StartY=-19.9603 StartZ=0 EndX=9.77779 EndY=-19.7529 EndZ=0
    g348: ArcOfCircle CenterX=9.70671 CenterY=-19.6208 CenterZ=0 NormalX=0 NormalY=0 NormalZ=1 AngleXU=-1.07712 Radius=0.15 StartAngle=0 EndAngle=1.5708
    g349: ArcOfCircle CenterX=11.2602 CenterY=-19.1777 CenterZ=0 NormalX=0 NormalY=0 NormalZ=-1 AngleXU=-0.255982 Radius=1.46929 StartAngle=0 EndAngle=0.255762
    g350: ArcOfCircle CenterX=10.3479 CenterY=-19.2296 CenterZ=0 NormalX=0 NormalY=0 NormalZ=-1 AngleXU=0.0923539 Radius=0.559359 StartAngle=0 EndAngle=1.96953
    g351: ArcOfCircle CenterX=9.80198 CenterY=-19.9624 CenterZ=0 NormalX=0 NormalY=0 NormalZ=-1 AngleXU=2.15445 Radius=1.46929 StartAngle=0 EndAngle=0.255762
    g352: ArcOfCircle CenterX=11.0276 CenterY=-18.91 CenterZ=0 NormalX=0 NormalY=0 NormalZ=1 AngleXU=-2.64791 Radius=0.15 StartAngle=0 EndAngle=1.5708
    g353: LineSegment StartX=11.0987 StartY=-19.0421 StartZ=0 EndX=11.5091 EndY=-18.7969 EndZ=0
    g354: ArcOfCircle CenterX=11.4264 CenterY=-18.6717 CenterZ=0 NormalX=0 NormalY=0 NormalZ=1 AngleXU=-0.987358 Radius=0.15 StartAngle=0 EndAngle=1.5708
    g355: ArcOfCircle CenterX=12.934 CenterY=-18.0911 CenterZ=0 NormalX=0 NormalY=0 NormalZ=-1 AngleXU=-0.345742 Radius=1.46929 StartAngle=0 EndAngle=0.255762
    g356: ArcOfCircle CenterX=12.03 CenterY=-18.2246 CenterZ=0 NormalX=0 NormalY=0 NormalZ=-1 AngleXU=0.00259414 Radius=0.559359 StartAngle=0 EndAngle=1.96953
    g357: ArcOfCircle CenterX=11.5519 CenterY=-19.0034 CenterZ=0 NormalX=0 NormalY=0 NormalZ=-1 AngleXU=2.0647 Radius=1.46929 StartAngle=0 EndAngle=0.255762
    g358: ArcOfCircle CenterX=12.6783 CenterY=-17.8454 CenterZ=0 NormalX=0 NormalY=0 NormalZ=1 AngleXU=-2.55815 Radius=0.15 StartAngle=0 EndAngle=1.5708
    g359: LineSegment StartX=12.7609 StartY=-17.9705 StartZ=0 EndX=13.1477 EndY=-17.6896 EndZ=0
    g360: ArcOfCircle CenterX=13.0541 CenterY=-17.5723 CenterZ=0 NormalX=0 NormalY=0 NormalZ=1 AngleXU=-0.897598 Radius=0.15 StartAngle=0 EndAngle=1.5708
    g361: ArcOfCircle CenterX=14.5036 CenterY=-16.8589 CenterZ=0 NormalX=0 NormalY=0 NormalZ=-1 AngleXU=-0.435501 Radius=1.46929 StartAngle=0 EndAngle=0.255762
    g362: ArcOfCircle CenterX=13.6152 CenterY=-17.0729 CenterZ=0 NormalX=0 NormalY=0 NormalZ=-1 AngleXU=-0.0871657 Radius=0.559359 StartAngle=0 EndAngle=1.96953
    g363: ArcOfCircle CenterX=13.2089 CenterY=-17.8914 CenterZ=0 NormalX=0 NormalY=0 NormalZ=-1 AngleXU=1.97494 Radius=1.46929 StartAngle=0 EndAngle=0.255762
    g364: ArcOfCircle CenterX=14.2269 CenterY=-16.6371 CenterZ=0 NormalX=0 NormalY=0 NormalZ=1 AngleXU=-2.46839 Radius=0.15 StartAngle=0 EndAngle=1.5708
    g365: LineSegment StartX=14.3204 StartY=-16.7543 StartZ=0 EndX=14.6804 EndY=-16.4398 EndZ=0
    g366: ArcOfCircle CenterX=14.5768 CenterY=-16.3314 CenterZ=0 NormalX=0 NormalY=0 NormalZ=1 AngleXU=-0.807838 Radius=0.15 StartAngle=0 EndAngle=1.5708
    g367: ArcOfCircle CenterX=15.9564 CenterY=-15.491 CenterZ=0 NormalX=0 NormalY=0 NormalZ=-1 AngleXU=-0.525261 Radius=1.46929 StartAngle=0 EndAngle=0.255762
    g368: ArcOfCircle CenterX=15.0908 CenterY=-15.7837 CenterZ=0 NormalX=0 NormalY=0 NormalZ=-1 AngleXU=-0.176925 Radius=0.559359 StartAngle=0 EndAngle=1.96953
    g369: ArcOfCircle CenterX=14.7595 CenterY=-16.6353 CenterZ=0 NormalX=0 NormalY=0 NormalZ=-1 AngleXU=1.88518 Radius=1.46929 StartAngle=0 EndAngle=0.255762
    g370: ArcOfCircle CenterX=15.661 CenterY=-15.2948 CenterZ=0 NormalX=0 NormalY=0 NormalZ=1 AngleXU=-2.37863 Radius=0.15 StartAngle=0 EndAngle=1.5708
    g371: LineSegment StartX=15.7646 StartY=-15.4032 StartZ=0 EndX=16.095 EndY=-15.0577 EndZ=0
    g372: ArcOfCircle CenterX=15.982 CenterY=-14.959 CenterZ=0 NormalX=0 NormalY=0 NormalZ=1 AngleXU=-0.718078 Radius=0.15 StartAngle=0 EndAngle=1.5708
    g373: ArcOfCircle CenterX=17.2808 CenterY=-13.9983 CenterZ=0 NormalX=0 NormalY=0 NormalZ=-1 AngleXU=-0.615021 Radius=1.46929 StartAngle=0 EndAngle=0.255762
    g374: ArcOfCircle CenterX=16.4449 CenterY=-14.3674 CenterZ=0 NormalX=0 NormalY=0 NormalZ=-1 AngleXU=-0.266685 Radius=0.559359 StartAngle=0 EndAngle=1.96953
    g375: ArcOfCircle CenterX=16.1912 CenterY=-15.2453 CenterZ=0 NormalX=0 NormalY=0 NormalZ=-1 AngleXU=1.79542 Radius=1.46929 StartAngle=0 EndAngle=0.255762
    g376: ArcOfCircle CenterX=16.9689 CenterY=-13.8294 CenterZ=0 NormalX=0 NormalY=0 NormalZ=1 AngleXU=-2.28887 Radius=0.15 StartAngle=0 EndAngle=1.5708
    g377: LineSegment StartX=17.0819 StartY=-13.9281 StartZ=0 EndX=17.3799 EndY=-13.5543 EndZ=0
    g378: ArcOfCircle CenterX=17.2586 CenterY=-13.4661 CenterZ=0 NormalX=0 NormalY=0 NormalZ=1 AngleXU=-0.628319 Radius=0.15 StartAngle=0 EndAngle=1.5708
    g379: ArcOfCircle CenterX=18.466 CenterY=-12.3929 CenterZ=0 NormalX=0 NormalY=0 NormalZ=-1 AngleXU=-0.704781 Radius=1.46929 StartAngle=0 EndAngle=0.255762
    g380: ArcOfCircle CenterX=17.6665 CenterY=-12.8355 CenterZ=0 NormalX=0 NormalY=0 NormalZ=-1 AngleXU=-0.356445 Radius=0.559359 StartAngle=0 EndAngle=1.96953
    g381: ArcOfCircle CenterX=17.4926 CenterY=-13.7326 CenterZ=0 NormalX=0 NormalY=0 NormalZ=-1 AngleXU=1.70566 Radius=1.46929 StartAngle=0 EndAngle=0.255762
    g382: ArcOfCircle CenterX=18.1403 CenterY=-12.2526 CenterZ=0 NormalX=0 NormalY=0 NormalZ=1 AngleXU=-2.19911 Radius=0.15 StartAngle=0 EndAngle=1.5708
    g383: LineSegment StartX=18.2616 StartY=-12.3408 StartZ=0 EndX=18.525 EndY=-11.9418 EndZ=0
    g384: ArcOfCircle CenterX=18.3962 CenterY=-11.8649 CenterZ=0 NormalX=0 NormalY=0 NormalZ=1 AngleXU=-0.538559 Radius=0.15 StartAngle=0 EndAngle=1.5708
    g385: ArcOfCircle CenterX=19.5025 CenterY=-10.6877 CenterZ=0 NormalX=0 NormalY=0 NormalZ=-1 AngleXU=-0.794541 Radius=1.46929 StartAngle=0 EndAngle=0.255762
    g386: ArcOfCircle CenterX=18.746 CenterY=-11.2002 CenterZ=0 NormalX=0 NormalY=0 NormalZ=-1 AngleXU=-0.446205 Radius=0.559359 StartAngle=0 EndAngle=1.96953
    g387: ArcOfCircle CenterX=18.6532 CenterY=-12.1093 CenterZ=0 NormalX=0 NormalY=0 NormalZ=-1 AngleXU=1.6159 Radius=1.46929 StartAngle=0 EndAngle=0.255762
    g388: ArcOfCircle CenterX=19.1656 CenterY=-10.5772 CenterZ=0 NormalX=0 NormalY=0 NormalZ=1 AngleXU=-2.10936 Radius=0.15 StartAngle=0 EndAngle=1.5708
    g389: LineSegment StartX=19.2943 StartY=-10.6542 StartZ=0 EndX=19.5209 EndY=-10.2332 EndZ=0
    g390: ArcOfCircle CenterX=19.3857 CenterY=-10.1681 CenterZ=0 NormalX=0 NormalY=0 NormalZ=1 AngleXU=-0.448799 Radius=0.15 StartAngle=0 EndAngle=1.5708
    g391: ArcOfCircle CenterX=20.3821 CenterY=-8.8965 CenterZ=0 NormalX=0 NormalY=0 NormalZ=-1 AngleXU=-0.8843 Radius=1.46929 StartAngle=0 EndAngle=0.255762
    g392: ArcOfCircle CenterX=19.6745 CenterY=-9.47474 CenterZ=0 NormalX=0 NormalY=0 NormalZ=-1 AngleXU=-0.535965 Radius=0.559359 StartAngle=0 EndAngle=1.96953
    g393: ArcOfCircle CenterX=19.6636 CenterY=-10.3885 CenterZ=0 NormalX=0 NormalY=0 NormalZ=-1 AngleXU=1.52614 Radius=1.46929 StartAngle=0 EndAngle=0.255762
    g394: ArcOfCircle CenterX=20.0365 CenterY=-8.81665 CenterZ=0 NormalX=0 NormalY=0 NormalZ=1 AngleXU=-2.0196 Radius=0.15 StartAngle=0 EndAngle=1.5708
    g395: LineSegment StartX=20.1717 StartY=-8.88173 StartZ=0 EndX=20.3596 EndY=-8.44215 EndZ=0
    g396: ArcOfCircle CenterX=20.2191 CenterY=-8.38945 CenterZ=0 NormalX=0 NormalY=0 NormalZ=1 AngleXU=-0.359039 Radius=0.15 StartAngle=0 EndAngle=1.5708
    g397: ArcOfCircle CenterX=21.0975 CenterY=-7.03365 CenterZ=0 NormalX=0 NormalY=0 NormalZ=-1 AngleXU=-0.97406 Radius=1.46929 StartAngle=0 EndAngle=0.255762
    g398: ArcOfCircle CenterX=20.4446 CenterY=-7.67299 CenterZ=0 NormalX=0 NormalY=0 NormalZ=-1 AngleXU=-0.625724 Radius=0.559359 StartAngle=0 EndAngle=1.96953
    g399: ArcOfCircle CenterX=20.5156 CenterY=-8.58402 CenterZ=0 NormalX=0 NormalY=0 NormalZ=-1 AngleXU=1.43638 Radius=1.46929 StartAngle=0 EndAngle=0.255762
    ... +21 more geometry lines
  constraints (1):
    c: Diameter(g420) = 8
FEATURE [PartDesign::Pad] Pad
  BaseFeature = -> Revolution001
  Direction = (0,0,-1)
  Length = 10.5
  Length2 = 10
  Placement = pos=(0,0,0) rot=(1,0,0;1.5708rad)
  Profile = -> SketchGear
  ReferenceAxis = -> SketchGear [N_Axis]
  Refine = true
  Suppressed = false
  Type = 0
FEATURE [Sketcher::SketchObject] Sketch039
  ArcFitTolerance = 1e-06
  AttachmentSupport = -> [Pad]
  FullyConstrained = true
  MakeInternals = false
  MapMode = 5
  Placement = pos=(0,4.2e-15,19) rot=(0,0,1;3.14159rad)
  expr: Constraints[1] = <<Spreadsheet>>.SecondShaftScrewHole
  expr: Constraints[2] = <<Spreadsheet>>.TopBearingHole / 2 - 3
  sketch-geometry (1):
    g0: Circle CenterX=0 CenterY=9.5 CenterZ=0 NormalX=0 NormalY=0 NormalZ=1 AngleXU=0 Radius=2
  constraints (3):
    c: PointOnObject(g0,g-2)
    c: Diameter(g0) = 4
    c: DistanceY(g-1,g0) = 9.5
FEATURE [PartDesign::Pocket] Pocket009
  BaseFeature = -> Pad
  Direction = (0,0,-1)
  Length = 10
  Length2 = 5
  Placement = pos=(0,0,0) rot=(1,0,0;1.5708rad)
  Profile = -> Sketch039
  ReferenceAxis = -> Sketch039 [N_Axis]
  Refine = true
  Suppressed = false
  Type = 0
FEATURE [PartDesign::PolarPattern] PolarPattern
  Angle = 360
  Axis = -> Sketch039 [N_Axis]
  BaseFeature = -> Pocket009
  Mode = 0
  Occurrences = 3
  Offset = 120
  Originals = -> [Pocket009]
  Placement = pos=(0,0,0) rot=(1,0,0;1.5708rad)
  Refine = true
  Suppressed = false
  TransformMode = 0
FEATURE [Sketcher::SketchObject] Sketch040
  ArcFitTolerance = 1e-06
  AttachmentSupport = -> [PolarPattern]
  FullyConstrained = true
  MakeInternals = false
  MapMode = 5
  Placement = pos=(0,0,-11.5) rot=(1,0,0;3.14159rad)
  sketch-geometry (2):
    g0: Circle CenterX=0 CenterY=0 CenterZ=0 NormalX=0 NormalY=0 NormalZ=1 AngleXU=0 Radius=20.15
    g1: Circle CenterX=0 CenterY=0 CenterZ=0 NormalX=0 NormalY=0 NormalZ=1 AngleXU=0 Radius=15
  constraints (4):
    c: Coincident(g0,g-1)
    c: Diameter(g0) = 40.3
    c: Coincident(g1,g0)
    c: Diameter(g1) = 30
FEATURE [PartDesign::Pad] Pad019
  BaseFeature = -> PolarPattern
  Direction = (0,0,-1)
  Length = 6
  Length2 = 10
  Placement = pos=(0,0,0) rot=(1,0,0;1.5708rad)
  Profile = -> Sketch040
  ReferenceAxis = -> Sketch040 [N_Axis]
  Refine = true
  Suppressed = false
  Type = 0
FEATURE [Sketcher::SketchObject] Sketch048
  ArcFitTolerance = 1e-06
  AttachmentSupport = -> [Pad019]
  FullyConstrained = false
  MakeInternals = false
  MapMode = 5
  Placement = pos=(0,4.2e-15,19) rot=(0,0,1;3.14159rad)
  sketch-geometry (7):
    g0: LineSegment StartX=3.5 StartY=6.06218 StartZ=0 EndX=-3.5 EndY=6.06218 EndZ=0
    g1: LineSegment StartX=-7 StartY=6.2e-15 StartZ=0 EndX=-3.5 EndY=-6.06218 EndZ=0
    g2: Circle [constr] CenterX=0 CenterY=0 CenterZ=0 NormalX=0 NormalY=0 NormalZ=1 AngleXU=0 Radius=7
    g3: ArcOfCircle CenterX=-5.25936 CenterY=3.03649 CenterZ=0 NormalX=0 NormalY=0 NormalZ=1 AngleXU=0 Radius=3.50002 StartAngle=1.04411 EndAngle=4.19188
    g4: ArcOfCircle CenterX=5.25395 CenterY=3.03337 CenterZ=0 NormalX=0 NormalY=0 NormalZ=1 AngleXU=0 Radius=3.5 StartAngle=5.23469 EndAngle=8.37888
    g5: ArcOfCircle CenterX=-2.27408e-10 CenterY=-6.07136 CenterZ=0 NormalX=0 NormalY=0 NormalZ=1 AngleXU=0 Radius=3.50001 StartAngle=3.13897 EndAngle=6.28581
    g6: LineSegment StartX=7 StartY=0 StartZ=0 EndX=3.5 EndY=-6.06218 EndZ=0
  constraints (14):
    c: PointOnObject(g0,g2)
    c: PointOnObject(g0,g2)
    c: PointOnObject(g1,g2)
    c: PointOnObject(g1,g2)
    c: PointOnObject(g4,g2)
    c: Radius(g2) = 7
    c: Coincident(g2,g-1)
    c: PointOnObject(g4,g-1)
    c: Coincident(g3,g0)
    c: Coincident(g5,g1)
    c: Coincident(g0,g4)
    c: Coincident(g1,g3)
    c: Coincident(g6,g4)
    c: Coincident(g6,g5)
FEATURE [PartDesign::Pocket] Pocket013
  BaseFeature = -> Pad019
  Direction = (0,0,-1)
  Length = 5
  Length2 = 5
  Placement = pos=(0,0,0) rot=(1,0,0;1.5708rad)
  Profile = -> Sketch048
  ReferenceAxis = -> Sketch048 [N_Axis]
  Refine = true
  Suppressed = false
  Type = 1
FEATURE [Sketcher::SketchObject] Sketch049
  ArcFitTolerance = 1e-06
  AttachmentSupport = -> [Pocket013]
  FullyConstrained = false
  MakeInternals = false
  MapMode = 5
  Placement = pos=(0,0,-11.5) rot=(1,0,0;3.14159rad)
  sketch-geometry (2):
    g0: ArcOfCircle CenterX=0 CenterY=0 CenterZ=0 NormalX=0 NormalY=0 NormalZ=1 AngleXU=0 Radius=20 StartAngle=6.02186 EndAngle=6.54546
    g1: ArcOfCircle CenterX=18.9986 CenterY=0.00904627 CenterZ=0 NormalX=0 NormalY=0 NormalZ=1 AngleXU=0 Radius=5.18625 StartAngle=4.77458 EndAngle=7.79274
  constraints (5):
    c: Radius(g0) = 20
    c: Angle(g0) = 0.523599
    c: Coincident(g0,g-1)
    c: Coincident(g1,g0)
    c: Coincident(g1,g0)
FEATURE [PartDesign::Pad] Pad021
  BaseFeature = -> Pocket013
  Direction = (0,0,-1)
  Length = 6
  Length2 = 10
  Placement = pos=(0,0,0) rot=(1,0,0;1.5708rad)
  Profile = -> Sketch049
  ReferenceAxis = -> Sketch049 [N_Axis]
  Refine = true
  Suppressed = false
  Type = 0
FEATURE [PartDesign::Body] Body002  label="MainShaft"
  AllowCompound = false
  Group = -> [Sketch,Revolution001,SketchGear,Pad,Sketch039,Pocket009,PolarPattern,Sketch040,Pad019,Sketch048,Pocket013,Sketch049,Pad021]
  Origin = -> Origin008
  Placement = pos=(5,-3.3e-15,6.96221) rot=(0,0,1;0rad)
  Tip = -> Pad021
COMPONENT P2 — recipe-attached ("Nema17Holder", modeled in this document).
Construction recipe (the document's own serialized feature program — sketch geometry with constraints, then the solid features built on it; lengths are millimeters unless a unit is written):

FEATURE [Sketcher::SketchObject] Sketch054
  ArcFitTolerance = 1e-06
  AttachmentSupport = -> [XY_Plane012]
  FullyConstrained = true
  MakeInternals = false
  MapMode = 5
  sketch-geometry (1):
    g0: Circle CenterX=0 CenterY=0 CenterZ=0 NormalX=0 NormalY=0 NormalZ=1 AngleXU=0 Radius=36.5
  constraints (2):
    c: Coincident(g0,g-1)
    c: Diameter(g0) = 73
FEATURE [PartDesign::Pad] Pad024
  Direction = (0,0,1)
  Length = 37
  Length2 = 10
  Profile = -> Sketch054
  ReferenceAxis = -> Sketch054 [N_Axis]
  Refine = true
  Suppressed = false
  Type = 0
FEATURE [Sketcher::SketchObject] Sketch055
  ArcFitTolerance = 1e-06
  AttachmentSupport = -> [Pad024]
  FullyConstrained = true
  MakeInternals = false
  MapMode = 5
  Placement = pos=(0,0,37) rot=(0,0,1;0rad)
  expr: Constraints[10] = <<Spreadsheet>>.StepperSize
  sketch-geometry (5):
    g0: LineSegment StartX=21 StartY=-21 StartZ=0 EndX=21 EndY=21 EndZ=0
    g1: LineSegment StartX=21 StartY=21 StartZ=0 EndX=-21 EndY=21 EndZ=0
    g2: LineSegment StartX=-21 StartY=21 StartZ=0 EndX=-21 EndY=-21 EndZ=0
    g3: LineSegment StartX=-21 StartY=-21 StartZ=0 EndX=21 EndY=-21 EndZ=0
    g4: GeomPoint [constr] X=0 Y=0 Z=0
  constraints (12):
    c: Coincident(g0,g1)
    c: Coincident(g1,g2)
    c: Coincident(g2,g3)
    c: Coincident(g3,g0)
    c: Vertical(g0)
    c: Vertical(g2)
    c: Horizontal(g1)
    c: Horizontal(g3)
    c: Symmetric(g2,g0,g4)
    c: Coincident(g4,g-1)
    c: Distance(g0,g0) = 42
    c: Equal(g1,g0)
FEATURE [PartDesign::Pocket] Pocket015
  BaseFeature = -> Pad024
  Direction = (0,0,-1)
  Length = 7
  Length2 = 5
  Profile = -> Sketch055
  ReferenceAxis = -> Sketch055 [N_Axis]
  Refine = true
  Suppressed = false
  Type = 0
FEATURE [Sketcher::SketchObject] Sketch056
  ArcFitTolerance = 1e-06
  AttachmentSupport = -> [Pocket015]
  FullyConstrained = true
  MakeInternals = false
  MapMode = 5
  Placement = pos=(0,0,0) rot=(1,0,0;3.14159rad)
  sketch-geometry (1):
    g0: Circle CenterX=0 CenterY=0 CenterZ=0 NormalX=0 NormalY=0 NormalZ=1 AngleXU=0 Radius=32.5
  constraints (2):
    c: Coincident(g0,g-1)
    c: Diameter(g0) = 65
FEATURE [PartDesign::Pocket] Pocket016
  BaseFeature = -> Pocket015
  Direction = (0,0,1)
  Length = 27
  Length2 = 5
  Profile = -> Sketch056
  ReferenceAxis = -> Sketch056 [N_Axis]
  Refine = true
  Suppressed = false
  Type = 0
FEATURE [Sketcher::SketchObject] Sketch057
  ArcFitTolerance = 1e-06
  AttachmentSupport = -> [Pocket016]
  FullyConstrained = true
  MakeInternals = false
  MapMode = 5
  Placement = pos=(0,0,27) rot=(1,0,0;3.14159rad)
  sketch-geometry (1):
    g0: Circle CenterX=0 CenterY=0 CenterZ=0 NormalX=0 NormalY=0 NormalZ=1 AngleXU=0 Radius=15
  constraints (2):
    c: Coincident(g0,g-1)
    c: Diameter(g0) = 30
FEATURE [PartDesign::Pocket] Pocket017
  BaseFeature = -> Pocket016
  Direction = (0,0,1)
  Length = 5
  Length2 = 5
  Profile = -> Sketch057
  ReferenceAxis = -> Sketch057 [N_Axis]
  Refine = true
  Suppressed = false
  Type = 0
FEATURE [Sketcher::SketchObject] Sketch058
  ArcFitTolerance = 1e-06
  AttachmentSupport = -> [Pocket017]
  FullyConstrained = true
  MakeInternals = false
  MapMode = 5
  Placement = pos=(0,0,27) rot=(1,0,0;3.14159rad)
  sketch-geometry (1):
    g0: Circle CenterX=-15.5 CenterY=15.5 CenterZ=0 NormalX=0 NormalY=0 NormalZ=1 AngleXU=0 Radius=1.5
  constraints (3):
    c: Diameter(g0) = 3
    c: DistanceX(g0,g-1) = 15.5
    c: DistanceY(g-1,g0) = 15.5
FEATURE [PartDesign::Pocket] Pocket018
  BaseFeature = -> Pocket017
  Direction = (0,0,1)
  Length = 5
  Length2 = 5
  Profile = -> Sketch058
  ReferenceAxis = -> Sketch058 [N_Axis]
  Refine = true
  Suppressed = false
  Type = 0
FEATURE [PartDesign::PolarPattern] PolarPattern004
  Angle = 360
  Axis = -> Sketch058 [N_Axis]
  BaseFeature = -> Pocket018
  Mode = 0
  Occurrences = 4
  Offset = 120
  Originals = -> [Pocket018]
  Refine = true
  Suppressed = false
  TransformMode = 0
FEATURE [Sketcher::SketchObject] Sketch059
  ArcFitTolerance = 1e-06
  AttachmentSupport = -> [PolarPattern004]
  FullyConstrained = true
  MakeInternals = false
  MapMode = 5
  Placement = pos=(0,0,0) rot=(1,0,0;3.14159rad)
  sketch-geometry (4):
    g0: LineSegment StartX=-45 StartY=27 StartZ=0 EndX=-45 EndY=-27 EndZ=0
    g1: LineSegment StartX=-45 StartY=-27 StartZ=0 EndX=-24.5611 EndY=-27 EndZ=0
    g2: LineSegment StartX=-45 StartY=27 StartZ=0 EndX=-24.5611 EndY=27 EndZ=0
    g3: ArcOfCircle CenterX=0 CenterY=0 CenterZ=0 NormalX=0 NormalY=0 NormalZ=1 AngleXU=0 Radius=36.5 StartAngle=2.30893 EndAngle=3.97426
  constraints (12):
    c: Vertical(g0)
    c: Coincident(g0,g1)
    c: Horizontal(g1)
    c: Coincident(g0,g2)
    c: Horizontal(g2)
    c: Diameter(g3) = 73
    c: Coincident(g3,g-1)
    c: Coincident(g3,g2)
    c: Coincident(g1,g3)
    c: Distance(g-1,g1) = 27
    c: Distance(g-1,g2) = 27
    c: Distance(g-2,g0) = 45
FEATURE [PartDesign::Pad] Pad025
  BaseFeature = -> PolarPattern004
  Direction = (0,0,-1)
  Length = 37
  Length2 = 10
  Profile = -> Sketch059
  ReferenceAxis = -> Sketch059 [N_Axis]
  Refine = true
  Reversed = true
  Suppressed = false
  Type = 0
FEATURE [Sketcher::SketchObject] Sketch060
  ArcFitTolerance = 1e-06
  AttachmentOffset = pos=(0,0,-5) rot=(0,0,1;0rad)
  AttachmentSupport = -> [Pad025]
  FullyConstrained = true
  MakeInternals = false
  MapMode = 5
  Placement = pos=(-40,0,0) rot=(0.57735,-0.57735,-0.57735;2.0944rad)
  sketch-geometry (5):
    g0: LineSegment StartX=21 StartY=6 StartZ=0 EndX=21 EndY=27 EndZ=0
    g1: LineSegment StartX=21 StartY=27 StartZ=0 EndX=-21 EndY=27 EndZ=0
    g2: LineSegment StartX=-21 StartY=27 StartZ=0 EndX=-21 EndY=6 EndZ=0
    g3: LineSegment StartX=-21 StartY=6 StartZ=0 EndX=21 EndY=6 EndZ=0
    g4: GeomPoint [constr] X=0 Y=16.5 Z=0
  constraints (13):
    c: Coincident(g0,g1)
    c: Coincident(g1,g2)
    c: Coincident(g2,g3)
    c: Coincident(g3,g0)
    c: Vertical(g0)
    c: Vertical(g2)
    c: Horizontal(g1)
    c: Horizontal(g3)
    c: Symmetric(g2,g0,g4)
    c: PointOnObject(g4,g-2)
    c: DistanceY(g-1,g4) = 16.5
    c: Distance(g0,g0) = 21
    c: Distance(g-2,g0) = 21
FEATURE [PartDesign::Pocket] Pocket019
  BaseFeature = -> Pad025
  Direction = (1,0,0)
  Length = 30
  Length2 = 5
  Profile = -> Sketch060
  ReferenceAxis = -> Sketch060 [N_Axis]
  Refine = true
  Suppressed = false
  Type = 0
FEATURE [Sketcher::SketchObject] Sketch061
  ArcFitTolerance = 1e-06
  AttachmentSupport = -> [Pocket019]
  FullyConstrained = true
  MakeInternals = false
  MapMode = 5
  Placement = pos=(-45,0,0) rot=(0.57735,-0.57735,-0.57735;2.0944rad)
  sketch-geometry (5):
    g0: LineSegment StartX=9 StartY=9 StartZ=0 EndX=9 EndY=24 EndZ=0
    g1: LineSegment StartX=9 StartY=24 StartZ=0 EndX=-9 EndY=24 EndZ=0
    g2: LineSegment StartX=-9 StartY=24 StartZ=0 EndX=-9 EndY=9 EndZ=0
    g3: LineSegment StartX=-9 StartY=9 StartZ=0 EndX=9 EndY=9 EndZ=0
    g4: GeomPoint [constr] X=1e-16 Y=16.5 Z=0
  constraints (13):
    c: Coincident(g0,g1)
    c: Coincident(g1,g2)
    c: Coincident(g2,g3)
    c: Coincident(g3,g0)
    c: Vertical(g0)
    c: Vertical(g2)
    c: Horizontal(g1)
    c: Horizontal(g3)
    c: Symmetric(g2,g0,g4)
    c: PointOnObject(g4,g-2)
    c: DistanceY(g-1,g4) = 16.5
    c: DistanceY(g2,g2) = 15
    c: DistanceX(g1,g1) = 18
FEATURE [PartDesign::Pocket] Pocket020
  BaseFeature = -> Pocket019
  Direction = (1,0,0)
  Length = 5
  Length2 = 5
  Profile = -> Sketch061
  ReferenceAxis = -> Sketch061 [N_Axis]
  Refine = true
  Suppressed = false
  Type = 0
FEATURE [Sketcher::SketchObject] Sketch062
  ArcFitTolerance = 1e-06
  AttachmentSupport = -> [Pocket020]
  FullyConstrained = true
  MakeInternals = false
  MapMode = 5
  Placement = pos=(0,0,0) rot=(1,0,0;3.14159rad)
  sketch-geometry (4):
    g0: LineSegment StartX=-40 StartY=21 StartZ=0 EndX=-40 EndY=-21 EndZ=0
    g1: LineSegment StartX=-40 StartY=-21 StartZ=0 EndX=-15 EndY=-21 EndZ=0
    g2: LineSegment StartX=-15 StartY=-21 StartZ=0 EndX=-15 EndY=21 EndZ=0
    g3: LineSegment StartX=-15 StartY=21 StartZ=0 EndX=-40 EndY=21 EndZ=0
  constraints (12):
    c: Coincident(g0,g1)
    c: Coincident(g1,g2)
    c: Coincident(g2,g3)
    c: Coincident(g3,g0)
    c: Vertical(g0)
    c: Vertical(g2)
    c: Horizontal(g1)
    c: Horizontal(g3)
    c: Distance(g-2,g0) = 40
    c: DistanceX(g3,g3) = 25
    c: Distance(g-1,g3) = 21
    c: Distance(g-1,g1) = 21
FEATURE [PartDesign::Pocket] Pocket021
  BaseFeature = -> Pocket020
  Direction = (0,0,1)
  Length = 10
  Length2 = 5
  Profile = -> Sketch062
  ReferenceAxis = -> Sketch062 [N_Axis]
  Refine = true
  Suppressed = false
  Type = 0
FEATURE [Sketcher::SketchObject] Sketch064
  ArcFitTolerance = 1e-06
  AttachmentSupport = -> [Pocket021]
  FullyConstrained = false
  MakeInternals = false
  MapMode = 5
  Placement = pos=(-45,0,0) rot=(0.57735,-0.57735,-0.57735;2.0944rad)
  sketch-geometry (4):
    g0: Circle CenterX=-14 CenterY=22 CenterZ=0 NormalX=0 NormalY=0 NormalZ=1 AngleXU=0 Radius=2.5
    g1: Circle CenterX=14 CenterY=22 CenterZ=0 NormalX=0 NormalY=0 NormalZ=1 AngleXU=0 Radius=2.5
    g2: Circle CenterX=14 CenterY=7.43628 CenterZ=0 NormalX=0 NormalY=0 NormalZ=1 AngleXU=0 Radius=2.5
    g3: Circle CenterX=-14 CenterY=7.43628 CenterZ=0 NormalX=0 NormalY=0 NormalZ=1 AngleXU=0 Radius=2.5
  constraints (11):
    c: Diameter(g0) = 5
    c: Diameter(g1) = 5
    c: Diameter(g2) = 5
    c: Diameter(g3) = 5
    c: Distance(g0,g-2) = 14
    c: DistanceX(g-1,g1) = 14
    c: Vertical(g3,g0)
    c: Vertical(g2,g1)
    c: Horizontal(g2,g3)
    c: Horizontal(g0,g1)
    c: DistanceY(g-1,g0) = 22
FEATURE [PartDesign::Pocket] Pocket023
  BaseFeature = -> Pocket021
  Direction = (1,0,0)
  Length = 5
  Length2 = 5
  Profile = -> Sketch064
  ReferenceAxis = -> Sketch064 [N_Axis]
  Refine = true
  Suppressed = false
  Type = 1
FEATURE [Sketcher::SketchObject] Sketch065
  ArcFitTolerance = 1e-06
  AttachmentSupport = -> [Pocket023]
  FullyConstrained = true
  MakeInternals = false
  MapMode = 5
  Placement = pos=(0,0,37) rot=(0,0,1;0rad)
  sketch-geometry (4):
    g0: Circle CenterX=27 CenterY=0 CenterZ=0 NormalX=0 NormalY=0 NormalZ=1 AngleXU=0 Radius=2.5
    g1: Circle CenterX=0 CenterY=27 CenterZ=0 NormalX=0 NormalY=0 NormalZ=1 AngleXU=0 Radius=2.5
    g2: Circle CenterX=0 CenterY=-27 CenterZ=0 NormalX=0 NormalY=0 NormalZ=1 AngleXU=0 Radius=2.5
    g3: Circle CenterX=-27 CenterY=0 CenterZ=0 NormalX=0 NormalY=0 NormalZ=1 AngleXU=0 Radius=2.5
  constraints (12):
    c: PointOnObject(g0,g-1)
    c: Diameter(g0) = 5
    c: DistanceX(g-1,g0) = 27
    c: PointOnObject(g1,g-2)
    c: PointOnObject(g2,g-2)
    c: Diameter(g1) = 5
    c: Diameter(g2) = 5
    c: DistanceY(g-1,g1) = 27
    c: DistanceY(g2,g-1) = 27
    c: PointOnObject(g3,g-1)
    c: Diameter(g3) = 5
    c: DistanceX(g3,g-1) = 27
FEATURE [PartDesign::Pocket] Pocket024
  BaseFeature = -> Pocket023
  Direction = (0,0,-1)
  Length = 5
  Length2 = 5
  Profile = -> Sketch065
  ReferenceAxis = -> Sketch065 [N_Axis]
  Refine = true
  Suppressed = false
  Type = 1
FEATURE [PartDesign::Body] Body005  label="Nema17Holder"
  AllowCompound = false
  Group = -> [Sketch054,Pad024,Sketch055,Pocket015,Sketch056,Pocket016,Sketch057,Pocket017,Sketch058,Pocket018,PolarPattern004,Sketch059,Pad025,Sketch060,Pocket019,Sketch061,Pocket020,Sketch062,Pocket021,Sketch064,Pocket023,Sketch065,Pocket024]
  Origin = -> Origin012
  Placement = pos=(260.223,1.57796e-05,-14.4622) rot=(0,0,1;0rad)
  Tip = -> Pocket024
COMPONENT P3 — recipe-attached ("SecondShaftUpper", modeled in this document).
Construction recipe (the document's own serialized feature program — sketch geometry with constraints, then the solid features built on it; lengths are millimeters unless a unit is written):

FEATURE [Sketcher::SketchObject] Sketch071
  ArcFitTolerance = 1e-06
  AttachmentSupport = -> [XY_Plane014]
  FullyConstrained = true
  MakeInternals = false
  MapMode = 5
  sketch-geometry (6):
    g0: Circle CenterX=0 CenterY=0 CenterZ=0 NormalX=0 NormalY=0 NormalZ=1 AngleXU=0 Radius=18.5
    g1: LineSegment StartX=40 StartY=-42 StartZ=0 EndX=40 EndY=42 EndZ=0
    g2: LineSegment StartX=40 StartY=42 StartZ=0 EndX=-40 EndY=42 EndZ=0
    g3: LineSegment StartX=-40 StartY=42 StartZ=0 EndX=-40 EndY=-42 EndZ=0
    g4: LineSegment StartX=-40 StartY=-42 StartZ=0 EndX=40 EndY=-42 EndZ=0
    g5: GeomPoint [constr] X=0 Y=0 Z=0
  constraints (14):
    c: Coincident(g0,g-1)
    c: Diameter(g0) = 37
    c: Coincident(g1,g2)
    c: Coincident(g2,g3)
    c: Coincident(g3,g4)
    c: Coincident(g4,g1)
    c: Vertical(g1)
    c: Vertical(g3)
    c: Horizontal(g2)
    c: Horizontal(g4)
    c: Symmetric(g3,g1,g5)
    c: Coincident(g5,g0)
    c: Distance(g-1,g2) = 42
    c: Distance(g-2,g1) = 40
FEATURE [PartDesign::Pad] Pad029
  Direction = (0,0,1)
  Length = 6
  Length2 = 10
  Profile = -> Sketch071
  ReferenceAxis = -> Sketch071 [N_Axis]
  Refine = true
  Suppressed = false
  Type = 0
FEATURE [Sketcher::SketchObject] Sketch072
  ArcFitTolerance = 1e-06
  AttachmentSupport = -> [Pad029]
  FullyConstrained = true
  MakeInternals = false
  MapMode = 5
  Placement = pos=(-40,0,0) rot=(0.57735,-0.57735,-0.57735;2.0944rad)
  sketch-geometry (6):
    g0: LineSegment StartX=27 StartY=0 StartZ=0 EndX=42 EndY=0 EndZ=0
    g1: LineSegment StartX=42 StartY=0 StartZ=0 EndX=42 EndY=-15 EndZ=0
    g2: LineSegment StartX=42 StartY=-15 StartZ=0 EndX=27 EndY=0 EndZ=0
    g3: LineSegment StartX=27 StartY=6 StartZ=0 EndX=42 EndY=6 EndZ=0
    g4: LineSegment StartX=42 StartY=6 StartZ=0 EndX=42 EndY=21 EndZ=0
    g5: LineSegment StartX=42 StartY=21 StartZ=0 EndX=27 EndY=6 EndZ=0
  constraints (18):
    c: PointOnObject(g0,g-1)
    c: PointOnObject(g0,g-1)
    c: Coincident(g0,g1)
    c: Vertical(g1)
    c: Coincident(g1,g2)
    c: Coincident(g2,g0)
    c: Horizontal(g3)
    c: Coincident(g3,g4)
    c: Vertical(g4)
    c: Coincident(g4,g5)
    c: Coincident(g5,g3)
    c: Distance(g-2,g4) = 42
    c: Vertical(g0,g3)
    c: Distance(g-1,g3) = 6
    c: Angle(g3,g5) = 0.785398
    c: Angle(g2,g0) = 0.785398
    c: Distance(g1,g1) = 15
    c: Equal(g1,g4)
FEATURE [PartDesign::Pad] Pad030
  BaseFeature = -> Pad029
  Direction = (-1,0,0)
  Length = 80
  Length2 = 10
  Profile = -> Sketch072
  ReferenceAxis = -> Sketch072 [N_Axis]
  Refine = true
  Reversed = true
  Suppressed = false
  Type = 0
FEATURE [Sketcher::SketchObject] Sketch073
  ArcFitTolerance = 1e-06
  AttachmentSupport = -> [Pad030]
  FullyConstrained = true
  MakeInternals = false
  MapMode = 5
  Placement = pos=(0,-42,0) rot=(1,0,0;1.5708rad)
  sketch-geometry (16):
    g0: ArcOfCircle CenterX=-32.5 CenterY=12 CenterZ=0 NormalX=0 NormalY=0 NormalZ=1 AngleXU=0 Radius=3 StartAngle=3.14159 EndAngle=6.28319
    g1: ArcOfCircle CenterX=-32.5 CenterY=15 CenterZ=0 NormalX=0 NormalY=0 NormalZ=1 AngleXU=0 Radius=3 StartAngle=0 EndAngle=3.14159
    g2: LineSegment StartX=-35.5 StartY=12 StartZ=0 EndX=-35.5 EndY=15 EndZ=0
    g3: LineSegment StartX=-29.5 StartY=12 StartZ=0 EndX=-29.5 EndY=15 EndZ=0
    g4: ArcOfCircle CenterX=32.5 CenterY=15 CenterZ=0 NormalX=0 NormalY=0 NormalZ=1 AngleXU=0 Radius=3 StartAngle=4e-16 EndAngle=3.14159
    g5: ArcOfCircle CenterX=32.5 CenterY=12 CenterZ=0 NormalX=0 NormalY=0 NormalZ=1 AngleXU=0 Radius=3 StartAngle=3.14159 EndAngle=6.28319
    g6: LineSegment StartX=35.5 StartY=15 StartZ=0 EndX=35.5 EndY=12 EndZ=0
    g7: LineSegment StartX=29.5 StartY=15 StartZ=0 EndX=29.5 EndY=12 EndZ=0
    g8: ArcOfCircle CenterX=-32.5 CenterY=-6 CenterZ=0 NormalX=0 NormalY=0 NormalZ=1 AngleXU=0 Radius=3 StartAngle=1e-16 EndAngle=3.14159
    g9: ArcOfCircle CenterX=-32.5 CenterY=-9 CenterZ=0 NormalX=0 NormalY=0 NormalZ=1 AngleXU=0 Radius=3 StartAngle=3.14159 EndAngle=6.28319
    g10: LineSegment StartX=-29.5 StartY=-6 StartZ=0 EndX=-29.5 EndY=-9 EndZ=0
    g11: LineSegment StartX=-35.5 StartY=-6 StartZ=0 EndX=-35.5 EndY=-9 EndZ=0
    g12: ArcOfCircle CenterX=32.5 CenterY=-6 CenterZ=0 NormalX=0 NormalY=0 NormalZ=1 AngleXU=0 Radius=3 StartAngle=1e-16 EndAngle=3.14159
    g13: ArcOfCircle CenterX=32.5 CenterY=-9 CenterZ=0 NormalX=0 NormalY=0 NormalZ=1 AngleXU=0 Radius=3 StartAngle=3.14159 EndAngle=6.28319
    g14: LineSegment StartX=35.5 StartY=-6 StartZ=0 EndX=35.5 EndY=-9 EndZ=0
    g15: LineSegment StartX=29.5 StartY=-6 StartZ=0 EndX=29.5 EndY=-9 EndZ=0
  constraints (40):
    c: Tangent(g0,g2) = 1.5708
    c: Tangent(g0,g3) = -1.5708
    c: Tangent(g1,g2) = 1.5708
    c: Tangent(g1,g3) = -1.5708
    c: Equal(g0,g1)
    c: Vertical(g3)
    c: Distance(g0,g1) = 3
    c: Radius(g0) = 3
    c: Tangent(g4,g6) = 1.5708
    c: Tangent(g4,g7) = -1.5708
    c: Tangent(g5,g6) = 1.5708
    c: Tangent(g5,g7) = -1.5708
    c: Equal(g4,g5)
    c: Vertical(g7)
    c: Distance(g4,g5) = 3
    c: Radius(g4) = 3
    c: Tangent(g8,g10) = 1.5708
    c: Tangent(g8,g11) = -1.5708
    c: Tangent(g9,g10) = 1.5708
    c: Tangent(g9,g11) = -1.5708
    c: Equal(g8,g9)
    c: Vertical(g11)
    c: Distance(g8,g9) = 3
    c: Radius(g8) = 3
    c: Tangent(g12,g14) = 1.5708
    c: Tangent(g12,g15) = -1.5708
    c: Tangent(g13,g14) = 1.5708
    c: Tangent(g13,g15) = -1.5708
    c: Equal(g12,g13)
    c: Vertical(g15)
    c: Distance(g12,g13) = 3
    c: Radius(g12) = 3
    c: Vertical(g0,g8)
    c: Vertical(g5,g12)
    c: Horizontal(g8,g12)
    c: Horizontal(g0,g5)
    c: Distance(g8,g-1) = 6
    c: Distance(g0,g-1) = 12
    c: DistanceX(g0,g-1) = 32.5
    c: DistanceX(g-1,g4) = 32.5
FEATURE [PartDesign::Pocket] Pocket027
  BaseFeature = -> Pad030
  Direction = (0,1,-2e-16)
  Length = 5
  Length2 = 5
  Profile = -> Sketch073
  ReferenceAxis = -> Sketch073 [N_Axis]
  Refine = true
  Suppressed = false
  Type = 1
FEATURE [Sketcher::SketchObject] Sketch074
  ArcFitTolerance = 1e-06
  AttachmentOffset = pos=(0,0,-5) rot=(0,0,1;0rad)
  AttachmentSupport = -> [Pocket027]
  FullyConstrained = false
  MakeInternals = false
  MapMode = 5
  Placement = pos=(0,-37,-1.1e-15) rot=(1,0,0;1.5708rad)
  sketch-geometry (16):
    g0: ArcOfCircle CenterX=-32.5 CenterY=15 CenterZ=0 NormalX=0 NormalY=0 NormalZ=1 AngleXU=0 Radius=5.5 StartAngle=1e-16 EndAngle=3.14159
    g1: ArcOfCircle CenterX=-32.5 CenterY=12 CenterZ=0 NormalX=0 NormalY=0 NormalZ=1 AngleXU=0 Radius=5.5 StartAngle=3.14159 EndAngle=6.28319
    g2: LineSegment StartX=-27 StartY=15 StartZ=0 EndX=-27 EndY=12 EndZ=0
    g3: LineSegment StartX=-38 StartY=15 StartZ=0 EndX=-38 EndY=12 EndZ=0
    g4: ArcOfCircle CenterX=32.5 CenterY=14.7943 CenterZ=0 NormalX=0 NormalY=0 NormalZ=1 AngleXU=0 Radius=5.5 StartAngle=1e-16 EndAngle=3.14159
    g5: ArcOfCircle CenterX=32.5 CenterY=11.7943 CenterZ=0 NormalX=0 NormalY=0 NormalZ=1 AngleXU=0 Radius=5.5 StartAngle=3.14159 EndAngle=6.28319
    g6: LineSegment StartX=38 StartY=14.7943 StartZ=0 EndX=38 EndY=11.7943 EndZ=0
    g7: LineSegment StartX=27 StartY=14.7943 StartZ=0 EndX=27 EndY=11.7943 EndZ=0
    g8: ArcOfCircle CenterX=32.5 CenterY=-6 CenterZ=0 NormalX=0 NormalY=0 NormalZ=1 AngleXU=0 Radius=5.5 StartAngle=1e-16 EndAngle=3.14159
    g9: ArcOfCircle CenterX=32.5 CenterY=-9 CenterZ=0 NormalX=0 NormalY=0 NormalZ=1 AngleXU=0 Radius=5.5 StartAngle=3.14159 EndAngle=6.28319
    g10: LineSegment StartX=38 StartY=-6 StartZ=0 EndX=38 EndY=-9 EndZ=0
    g11: LineSegment StartX=27 StartY=-6 StartZ=0 EndX=27 EndY=-9 EndZ=0
    g12: ArcOfCircle CenterX=-32.5 CenterY=-6 CenterZ=0 NormalX=0 NormalY=0 NormalZ=1 AngleXU=0 Radius=5.5 StartAngle=2e-16 EndAngle=3.14159
    g13: ArcOfCircle CenterX=-32.5 CenterY=-9 CenterZ=0 NormalX=0 NormalY=0 NormalZ=1 AngleXU=0 Radius=5.5 StartAngle=3.14159 EndAngle=6.28319
    g14: LineSegment StartX=-27 StartY=-6 StartZ=0 EndX=-27 EndY=-9 EndZ=0
    g15: LineSegment StartX=-38 StartY=-6 StartZ=0 EndX=-38 EndY=-9 EndZ=0
  constraints (39):
    c: Tangent(g0,g2) = 1.5708
    c: Tangent(g0,g3) = -1.5708
    c: Tangent(g1,g2) = 1.5708
    c: Tangent(g1,g3) = -1.5708
    c: Equal(g0,g1)
    c: Radius(g0) = 5.5
    c: Vertical(g2)
    c: DistanceY(g2,g2) = 3
    c: DistanceX(g0,g-1) = 32.5
    c: Distance(g1,g-1) = 12
    c: Tangent(g4,g6) = 1.5708
    c: Tangent(g4,g7) = -1.5708
    c: Tangent(g5,g6) = 1.5708
    c: Tangent(g5,g7) = -1.5708
    c: Equal(g4,g5)
    c: Vertical(g7)
    c: Distance(g4,g5) = 3
    c: Radius(g4) = 5.5
    c: Tangent(g8,g10) = 1.5708
    c: Tangent(g8,g11) = -1.5708
    c: Tangent(g9,g10) = 1.5708
    c: Tangent(g9,g11) = -1.5708
    c: Equal(g8,g9)
    c: Vertical(g11)
    c: Distance(g8,g9) = 3
    c: Radius(g8) = 5.5
    c: Tangent(g12,g14) = 1.5708
    c: Tangent(g12,g15) = -1.5708
    c: Tangent(g13,g14) = 1.5708
    c: Tangent(g13,g15) = -1.5708
    c: Equal(g12,g13)
    c: Vertical(g15)
    c: Distance(g12,g13) = 3
    c: Radius(g12) = 5.5
    c: DistanceX(g-1,g4) = 32.5
    c: Distance(g8,g-1) = 6
    c: Vertical(g4,g8)
    c: Horizontal(g8,g12)
    c: Vertical(g12,g0)
FEATURE [PartDesign::Pocket] Pocket028
  BaseFeature = -> Pocket027
  Direction = (0,1,-2e-16)
  Length = 5
  Length2 = 5
  Profile = -> Sketch074
  ReferenceAxis = -> Sketch074 [N_Axis]
  Refine = true
  Suppressed = false
  Type = 1
FEATURE [PartDesign::Body] Body007  label="SecondShaftUpper"
  AllowCompound = false
  Group = -> [Sketch071,Pad029,Sketch072,Pad030,Sketch073,Pocket027,Sketch074,Pocket028]
  Origin = -> Origin014
  Placement = pos=(0,-1.22786e-05,103) rot=(0,0,1;0rad)
  Tip = -> Pocket028
COMPONENT P4 — recipe-attached ("BeltMain", modeled in this document).
Construction recipe (the document's own serialized feature program — sketch geometry with constraints, then the solid features built on it; lengths are millimeters unless a unit is written):

FEATURE [Sketcher::SketchObject] Sketch095
  ArcFitTolerance = 1e-06
  AttachmentSupport = -> [XY_Plane016]
  FullyConstrained = false
  MakeInternals = false
  MapMode = 5
  sketch-geometry (6):
    g0: ArcOfCircle CenterX=0 CenterY=0 CenterZ=0 NormalX=0 NormalY=0 NormalZ=1 AngleXU=0 Radius=22.5 StartAngle=1.29412 EndAngle=4.97683
    g1: ArcOfCircle CenterX=255 CenterY=0 CenterZ=0 NormalX=0 NormalY=0 NormalZ=1 AngleXU=0 Radius=6.5 StartAngle=4.70438 EndAngle=7.86199
    g2: LineSegment StartX=5.88074 StartY=-21.7179 StartZ=0 EndX=67.6209 EndY=-5 EndZ=0
    g3: LineSegment StartX=67.6209 StartY=-5 StartZ=0 EndX=254.948 EndY=-6.49979 EndZ=0
    g4: LineSegment StartX=254.948 StartY=6.49979 StartZ=0 EndX=67.6209 EndY=5 EndZ=0
    g5: LineSegment StartX=6.14609 StartY=21.6443 StartZ=0 EndX=67.6209 EndY=5 EndZ=0
  constraints (15):
    c: Diameter(g0) = 45
    c: Coincident(g0,g-1)
    c: Diameter(g1) = 13
    c: DistanceX(g-1,g1) = 255
    c: Coincident(g2,g3)
    c: Distance(g0,g2) = 22.5
    c: Coincident(g0,g2)
    c: Tangent(g1,g3) = -1.5708
    c: Horizontal(g1,g0)
    c: Tangent(g1,g4) = -1.5708
    c: Coincident(g5,g0)
    c: Coincident(g5,g4)
    c: Distance(g4,g-1) = 5
    c: Distance(g2,g-1) = 5
    c: Vertical(g2,g4)
FEATURE [PartDesign::Pad] Pad037
  Direction = (0,0,1)
  Length = 6
  Length2 = 10
  Profile = -> Sketch095
  ReferenceAxis = -> Sketch095 [N_Axis]
  Refine = true
  Suppressed = false
  Type = 0
FEATURE [PartDesign::Thickness] Thickness
  Base = -> Pad037 [Face7,Face8]
  BaseFeature = -> Pad037
  Intersection = false
  Join = 0
  Mode = 0
  Refine = true
  Reversed = true
  SupportTransform = false
  Suppressed = false
  Value = 1
FEATURE [PartDesign::Body] Body009  label="BeltMain"
  AllowCompound = false
  Group = -> [Sketch095,Pad037,Thickness]
  Origin = -> Origin016
  Placement = pos=(5,0,-0.3) rot=(0,0,1;0rad)
  Tip = -> Thickness
COMPONENT P5 — recipe-attached ("FastenBeltHolder", modeled in this document).
Construction recipe (the document's own serialized feature program — sketch geometry with constraints, then the solid features built on it; lengths are millimeters unless a unit is written):

FEATURE [Sketcher::SketchObject] Sketch097
  ArcFitTolerance = 1e-06
  AttachmentSupport = -> [XY_Plane017]
  FullyConstrained = false
  MakeInternals = false
  MapMode = 5
  sketch-geometry (22):
    g0: LineSegment StartX=18.5159 StartY=20.5421 StartZ=0 EndX=-18.5159 EndY=20.5421 EndZ=0
    g1: LineSegment StartX=-18.5159 StartY=20.5421 StartZ=0 EndX=-18.5159 EndY=10 EndZ=0
    g2: LineSegment StartX=-18.501 StartY=-20.5421 StartZ=0 EndX=18.5159 EndY=-20.5421 EndZ=0
    g3: LineSegment StartX=18.5159 StartY=-20.5421 StartZ=0 EndX=18.5159 EndY=20.5421 EndZ=0
    g4: ArcOfCircle CenterX=-12.5 CenterY=15 CenterZ=0 NormalX=0 NormalY=0 NormalZ=1 AngleXU=0 Radius=1.75 StartAngle=1.5708 EndAngle=4.71239
    g5: ArcOfCircle CenterX=-4.5 CenterY=15 CenterZ=0 NormalX=0 NormalY=0 NormalZ=1 AngleXU=0 Radius=1.75 StartAngle=4.71239 EndAngle=7.85398
    g6: LineSegment StartX=-12.5 StartY=16.75 StartZ=0 EndX=-4.5 EndY=16.75 EndZ=0
    g7: LineSegment StartX=-12.5 StartY=13.25 StartZ=0 EndX=-4.5 EndY=13.25 EndZ=0
    g8: ArcOfCircle CenterX=-12.5 CenterY=-15 CenterZ=0 NormalX=0 NormalY=0 NormalZ=1 AngleXU=0 Radius=1.75 StartAngle=1.5708 EndAngle=4.71239
    g9: ArcOfCircle CenterX=-4.5 CenterY=-15 CenterZ=0 NormalX=0 NormalY=0 NormalZ=1 AngleXU=0 Radius=1.75 StartAngle=4.71239 EndAngle=7.85398
    g10: LineSegment StartX=-12.5 StartY=-13.25 StartZ=0 EndX=-4.5 EndY=-13.25 EndZ=0
    g11: LineSegment StartX=-12.5 StartY=-16.75 StartZ=0 EndX=-4.5 EndY=-16.75 EndZ=0
    g12: ArcOfCircle CenterX=7.19115 CenterY=0 CenterZ=0 NormalX=0 NormalY=0 NormalZ=1 AngleXU=0 Radius=1.75 StartAngle=1.5708 EndAngle=4.71239
    g13: ArcOfCircle CenterX=15.1911 CenterY=-1e-16 CenterZ=0 NormalX=0 NormalY=0 NormalZ=1 AngleXU=0 Radius=1.75 StartAngle=4.71239 EndAngle=7.85398
    g14: LineSegment StartX=7.19115 StartY=1.75 StartZ=0 EndX=15.1911 EndY=1.75 EndZ=0
    g15: LineSegment StartX=7.19115 StartY=-1.75 StartZ=0 EndX=15.1911 EndY=-1.75 EndZ=0
    g16: Circle CenterX=5 CenterY=-11 CenterZ=0 NormalX=0 NormalY=0 NormalZ=1 AngleXU=0 Radius=2.75
    g17: Circle CenterX=5 CenterY=11 CenterZ=0 NormalX=0 NormalY=0 NormalZ=1 AngleXU=0 Radius=2.75
    g18: LineSegment StartX=-18.5159 StartY=10 StartZ=0 EndX=-3.5159 EndY=10 EndZ=0
    g19: LineSegment StartX=-3.5159 StartY=10 StartZ=0 EndX=-3.5159 EndY=-10 EndZ=0
    g20: LineSegment StartX=-3.5159 StartY=-10 StartZ=0 EndX=-18.501 EndY=-10 EndZ=0
    g21: LineSegment StartX=-18.501 StartY=-10 StartZ=0 EndX=-18.501 EndY=-20.5421 EndZ=0
  constraints (55):
    c: Coincident(g0,g1)
    c: Coincident(g21,g2)
    c: Coincident(g2,g3)
    c: Coincident(g3,g0)
    c: Horizontal(g0)
    c: Horizontal(g2)
    c: Vertical(g1)
    c: Vertical(g3)
    c: Tangent(g4,g6) = 1.5708
    c: Tangent(g4,g7) = -1.5708
    c: Tangent(g5,g6) = 1.5708
    c: Tangent(g5,g7) = -1.5708
    c: Equal(g4,g5)
    c: Horizontal(g7)
    c: Distance(g4,g5) = 8
    c: Radius(g4) = 1.75
    c: Tangent(g8,g10) = 1.5708
    c: Tangent(g8,g11) = -1.5708
    c: Tangent(g9,g10) = 1.5708
    c: Tangent(g9,g11) = -1.5708
    c: Equal(g8,g9)
    c: Horizontal(g11)
    c: Distance(g8,g9) = 8
    c: Radius(g8) = 1.75
    c: Vertical(g8,g4)
    c: DistanceX(g4,g-1) = 12.5
    c: Symmetric(g0,g2,g-1)
    c: Distance(g8,g-1) = 15
    c: DistanceY(g-1,g4) = 15
    c: Tangent(g12,g14) = 1.5708
    c: Tangent(g12,g15) = -1.5708
    c: Tangent(g13,g14) = 1.5708
    c: Tangent(g13,g15) = -1.5708
    c: Equal(g12,g13)
    c: Horizontal(g15)
    c: Distance(g12,g13) = 8
    c: Radius(g12) = 1.75
    c: PointOnObject(g12,g-1)
    c: Diameter(g16) = 5.5
    c: DistanceY(g16,g-1) = 11
    c: Distance(g16,g-2) = 5
    c: Diameter(g17) = 5.5
    c: DistanceX(g-1,g17) = 5
    c: DistanceY(g-1,g17) = 11
    c: Horizontal(g18)
    c: Coincident(g18,g19)
    c: Vertical(g19)
    c: Coincident(g19,g20)
    c: PointOnObject(g20,g21)
    c: Horizontal(g20)
    c: Coincident(g1,g18)
    c: PointOnObject(g21,g20)
    c: DistanceX(g18,g18) = 15
    c: Distance(g-1,g18) = 10
    c: Distance(g-1,g20) = 10
FEATURE [PartDesign::Pad] Pad038
  Direction = (0,0,1)
  Length = 8
  Length2 = 10
  Profile = -> Sketch097
  ReferenceAxis = -> Sketch097 [N_Axis]
  Refine = true
  Suppressed = false
  Type = 0
FEATURE [PartDesign::Fillet] Fillet
  Base = -> Pad038 [Edge1,Edge20]
  BaseFeature = -> Pad038
  Radius = 15
  Refine = true
  SupportTransform = false
  Suppressed = false
  UseAllEdges = false
FEATURE [PartDesign::Body] Body010  label="FastenBeltHolder"
  AllowCompound = false
  Group = -> [Sketch097,Pad038,Fillet]
  Origin = -> Origin017
  Placement = pos=(77.7,0,16.9) rot=(0,1,0;3.14159rad)
  Tip = -> Fillet
COMPONENT P6 — geometry summary ("Limit Switch v004"; no construction recipe available for this part):
  bounding box: 16.8 x 15.7 x 9.8 mm
  tessellated surface: 968 triangles
  volume: 472 mm^3 (18% of its bounding box)
COMPONENT P7 — recipe-attached ("Bearing6808-2RS001", modeled in this document).
Construction recipe (the document's own serialized feature program — sketch geometry with constraints, then the solid features built on it; lengths are millimeters unless a unit is written):

FEATURE [Sketcher::SketchObject] Sketch041
  ArcFitTolerance = 0
  AttachmentSupport = -> [YZ_Plane009]
  FullyConstrained = false
  MakeInternals = false
  MapMode = 5
  Placement = pos=(0,0,0) rot=(0.57735,0.57735,0.57735;2.0944rad)
  expr: Constraints[16] = <<Spreadsheet>>.BottomBearingInnerDiameter / 2
  expr: Constraints[17] = <<Spreadsheet>>.BottomBearingOuterDiameter / 2
  expr: Constraints[1] = <<Spreadsheet>>.BottomBearingHeight
  sketch-geometry (12):
    g0: LineSegment StartX=20 StartY=3.5 StartZ=0 EndX=20 EndY=-3.5 EndZ=0
    g1: LineSegment StartX=20 StartY=3.5 StartZ=0 EndX=21.25 EndY=3.5 EndZ=0
    g2: LineSegment StartX=21.25 StartY=3.5 StartZ=0 EndX=21.5 EndY=3.25 EndZ=0
    g3: LineSegment StartX=21.5 StartY=3.25 StartZ=0 EndX=24.75 EndY=3.25 EndZ=0
    g4: LineSegment StartX=24.75 StartY=3.25 StartZ=0 EndX=25 EndY=3.5 EndZ=0
    g5: LineSegment StartX=25 StartY=3.5 StartZ=0 EndX=26 EndY=3.5 EndZ=0
    g6: LineSegment StartX=26 StartY=3.5 StartZ=0 EndX=26 EndY=-3.5 EndZ=0
    g7: LineSegment StartX=20 StartY=-3.5 StartZ=0 EndX=21.25 EndY=-3.5 EndZ=0
    g8: LineSegment StartX=21.25 StartY=-3.5 StartZ=0 EndX=21.5707 EndY=-3.19528 EndZ=0
    g9: LineSegment StartX=21.5707 StartY=-3.19528 StartZ=0 EndX=24.8207 EndY=-3.19528 EndZ=0
    g10: LineSegment StartX=24.8207 StartY=-3.19528 StartZ=0 EndX=25 EndY=-3.5 EndZ=0
    g11: LineSegment StartX=25 StartY=-3.5 StartZ=0 EndX=26 EndY=-3.5 EndZ=0
  constraints (34):
    c: Symmetric(g0,g0,g-1)
    c: DistanceY(g0,g0) = 7
    c: Coincident(g1,g0)
    c: Horizontal(g1)
    c: Coincident(g2,g1)
    c: Coincident(g3,g2)
    c: Horizontal(g3)
    c: Coincident(g4,g3)
    c: Coincident(g5,g4)
    c: Horizontal(g5)
    c: Coincident(g6,g5)
    c: Vertical(g6)
    c: Angle(g1,g2) = 2.35619
    c: DistanceY(g3,g5) = 0.25
    c: Horizontal(g4,g1)
    c: Equal(g4,g2)
    c: DistanceX(g-1,g0) = 20
    c: DistanceX(g-1,g6) = 26
    c: DistanceX(g1,g1) = 1.25
    c: DistanceX(g5,g5) = 1
    c: Equal(g0,g6)
    c: Coincident(g7,g0)
    c: Horizontal(g7)
    c: Equal(g1,g7)
    c: Coincident(g8,g7)
    c: Coincident(g9,g8)
    c: Horizontal(g9)
    c: Coincident(g10,g9)
    c: Coincident(g11,g10)
    c: Coincident(g11,g6)
    c: Horizontal(g11)
    c: Equal(g5,g11)
    c: Equal(g10,g4)
    c: Equal(g3,g9)
FEATURE [PartDesign::Revolution] Revolution002
  Angle = 360
  Angle2 = 60
  Axis = (0,0,1)
  Base = (0,0,0)
  Placement = pos=(0,0,0) rot=(1,1,1;2.0944rad)
  Profile = -> Sketch041
  ReferenceAxis = -> Sketch041 [V_Axis]
  Reversed = true
  Suppressed = false
  Type = 0
FEATURE [PartDesign::Chamfer] Chamfer001
  Angle = 45
  Base = -> Revolution002 [Edge11,Edge1,Edge10,Edge2]
  BaseFeature = -> Revolution002
  ChamferType = 0
  FlipDirection = false
  Placement = pos=(0,0,0) rot=(1,1,1;2.0944rad)
  Size = 0.25
  Size2 = 1
  SupportTransform = false
  Suppressed = false
  UseAllEdges = false
FEATURE [PartDesign::Body] Body003  label="Bearing6808-2RS"
  AllowCompound = true
  Group = -> [Sketch041,Revolution002,Chamfer001]
  Origin = -> Origin009
  Placement = pos=(5,-1.2e-15,-21) rot=(0,0,1;0rad)
  Tip = -> Chamfer001
COMPONENT P8 — recipe-attached ("Bottom001", modeled in this document).
Construction recipe (the document's own serialized feature program — sketch geometry with constraints, then the solid features built on it; lengths are millimeters unless a unit is written):

FEATURE [Sketcher::SketchObject] Sketch042
  ArcFitTolerance = 1e-06
  AttachmentSupport = -> [YZ_Plane010]
  FullyConstrained = true
  MakeInternals = false
  MapMode = 5
  Placement = pos=(0,0,0) rot=(0.57735,0.57735,0.57735;2.0944rad)
  expr: Constraints[16] = <<Spreadsheet>>.BottomBearingOuterDiameter / 2
  expr: Constraints[17] = <<Spreadsheet>>.TopDiameter / 2
  expr: Constraints[18] = <<Spreadsheet>>.TopGearHoleDiameter / 2
  sketch-geometry (8):
    g0: LineSegment StartX=26 StartY=-18 StartZ=0 EndX=27 EndY=-18 EndZ=0
    g1: LineSegment StartX=27 StartY=-18 StartZ=0 EndX=27 EndY=-22 EndZ=0
    g2: LineSegment StartX=27 StartY=-22 StartZ=0 EndX=32 EndY=-22 EndZ=0
    g3: LineSegment StartX=32 StartY=-22 StartZ=0 EndX=32 EndY=-27 EndZ=0
    g4: LineSegment StartX=26 StartY=-18 StartZ=0 EndX=26 EndY=-25.5 EndZ=0
    g5: LineSegment StartX=26 StartY=-25.5 StartZ=0 EndX=0 EndY=-25.5 EndZ=0
    g6: LineSegment StartX=0 StartY=-25.5 StartZ=0 EndX=0 EndY=-27 EndZ=0
    g7: LineSegment StartX=0 StartY=-27 StartZ=0 EndX=32 EndY=-27 EndZ=0
  constraints (24):
    c: Horizontal(g0)
    c: Coincident(g0,g1)
    c: Vertical(g1)
    c: Coincident(g1,g2)
    c: Horizontal(g2)
    c: Coincident(g2,g3)
    c: Vertical(g3)
    c: Coincident(g0,g4)
    c: Vertical(g4)
    c: Coincident(g4,g5)
    c: Horizontal(g5)
    c: Coincident(g5,g6)
    c: Vertical(g6)
    c: Coincident(g6,g7)
    c: Coincident(g7,g3)
    c: Horizontal(g7)
    c: Distance(g-2,g4) = 26
    c: Distance(g-2,g3) = 32
    c: Distance(g-2,g1) = 27
    c: Distance(g7,g0) = 9
    c: Vertical(g-1,g5)
    c: Distance(g-1,g2) = 22
    c: DistanceY(g3,g3) = 5
    c: Distance(g6,g6) = 1.5
FEATURE [PartDesign::Revolution] Revolution003
  Angle = 360
  Angle2 = 60
  Axis = (0,0,1)
  Base = (0,0,0)
  Placement = pos=(0,0,0) rot=(1,1,1;2.0944rad)
  Profile = -> Sketch042
  ReferenceAxis = -> Sketch042 [V_Axis]
  Refine = true
  Reversed = true
  Suppressed = false
  Type = 0
FEATURE [Sketcher::SketchObject] Sketch045
  ArcFitTolerance = 1e-06
  AttachmentSupport = -> [Revolution003]
  FullyConstrained = true
  MakeInternals = false
  MapMode = 5
  Placement = pos=(9e-15,-3e-15,-27) rot=(0.707107,0.707107,0;3.14159rad)
  expr: Constraints[1] = <<Spreadsheet>>.StepperScrewHole
  sketch-geometry (1):
    g0: Circle CenterX=0 CenterY=29.53 CenterZ=0 NormalX=0 NormalY=0 NormalZ=1 AngleXU=0 Radius=1.5
  constraints (3):
    c: PointOnObject(g0,g-2)
    c: Diameter(g0) = 3
    c: DistanceY(g-1,g0) = 29.53
FEATURE [PartDesign::Pocket] Pocket012
  BaseFeature = -> Revolution003
  Direction = (0,0,1)
  Length = 5
  Length2 = 5
  Placement = pos=(0,0,0) rot=(1,1,1;2.0944rad)
  Profile = -> Sketch045
  ReferenceAxis = -> Sketch045 [N_Axis]
  Refine = true
  Suppressed = false
  Type = 1
FEATURE [PartDesign::PolarPattern] PolarPattern002
  Angle = 360
  Axis = -> Sketch045 [N_Axis]
  BaseFeature = -> Pocket012
  Mode = 0
  Occurrences = 3
  Offset = 120
  Originals = -> [Pocket012]
  Placement = pos=(0,0,0) rot=(1,1,1;2.0944rad)
  Refine = true
  Suppressed = false
  TransformMode = 0
FEATURE [Sketcher::SketchObject] Sketch051
  ArcFitTolerance = 1e-06
  AttachmentSupport = -> [PolarPattern002]
  FullyConstrained = true
  MakeInternals = false
  MapMode = 5
  Placement = pos=(1.8e-14,-6e-15,-27) rot=(0.707107,0.707107,0;3.14159rad)
  sketch-geometry (4):
    g0: ArcOfCircle CenterX=0 CenterY=0 CenterZ=0 NormalX=0 NormalY=0 NormalZ=1 AngleXU=0 Radius=27 StartAngle=3.87822 EndAngle=5.54656
    g1: ArcOfCircle CenterX=0 CenterY=-18 CenterZ=0 NormalX=0 NormalY=0 NormalZ=1 AngleXU=0 Radius=27 StartAngle=3.87822 EndAngle=5.54656
    g2: LineSegment StartX=-20 StartY=-18.1384 StartZ=0 EndX=-20 EndY=-36.1384 EndZ=0
    g3: LineSegment StartX=20 StartY=-18.1384 StartZ=0 EndX=20 EndY=-36.1384 EndZ=0
  constraints (13):
    c: Coincident(g0,g-1)
    c: Radius(g1) = 27
    c: Coincident(g2,g0)
    c: Coincident(g2,g1)
    c: Vertical(g2)
    c: Coincident(g3,g0)
    c: Coincident(g3,g1)
    c: Vertical(g3)
    c: Radius(g0) = 27
    c: Vertical(g1,g0)
    c: DistanceY(g1,g-1) = 18
    c: Distance(g-2,g2) = 20
    c: Distance(g-2,g3) = 20
FEATURE [PartDesign::Pad] Pad022
  BaseFeature = -> PolarPattern002
  Direction = (0,0,-1)
  Length = 9
  Length2 = 10
  Placement = pos=(0,0,0) rot=(1,1,1;2.0944rad)
  Profile = -> Sketch051
  ReferenceAxis = -> Sketch051 [N_Axis]
  Refine = true
  Reversed = true
  Suppressed = false
  Type = 0
FEATURE [Sketcher::SketchObject] Sketch052
  ArcFitTolerance = 1e-06
  AttachmentSupport = -> [Pad022]
  FullyConstrained = false
  MakeInternals = false
  MapMode = 5
  Placement = pos=(2e-15,-1.12e-14,-18) rot=(0,0,-1;1.5708rad)
  sketch-geometry (4):
    g0: LineSegment StartX=-6.5 StartY=-25 StartZ=0 EndX=-6.5 EndY=-35.2461 EndZ=0
    g1: ArcOfCircle CenterX=0 CenterY=0 CenterZ=0 NormalX=0 NormalY=0 NormalZ=1 AngleXU=0 Radius=25.8312 StartAngle=4.19622 EndAngle=4.45802
    g2: ArcOfCircle CenterX=-1e-06 CenterY=-10.2461 CenterZ=0 NormalX=0 NormalY=0 NormalZ=1 AngleXU=0 Radius=25.8312 StartAngle=4.19622 EndAngle=4.45802
    g3: LineSegment StartX=-12.749 StartY=-22.4658 StartZ=0 EndX=-12.749 EndY=-32.712 EndZ=0
  constraints (6):
    c: Vertical(g0)
    c: Angle(g1) = 0.261799
    c: Coincident(g1,g3)
    c: Coincident(g2,g3)
    c: Coincident(g0,g1)
    c: Coincident(g0,g2)
FEATURE [PartDesign::Pad] Pad023
  BaseFeature = -> Pad022
  Direction = (0,0,1)
  Length = 6
  Length2 = 10
  Placement = pos=(0,0,0) rot=(1,1,1;2.0944rad)
  Profile = -> Sketch052
  ReferenceAxis = -> Sketch052 [N_Axis]
  Refine = true
  Suppressed = false
  Type = 0
FEATURE [Sketcher::SketchObject] Sketch053
  ArcFitTolerance = 1e-06
  FullyConstrained = true
  MakeInternals = false
  MapMode = 5
  Placement = pos=(1.33e-14,-1.27e-14,-17.5451) rot=(0,0,-1;1.5708rad)
  sketch-geometry (2):
    g0: Circle CenterX=3.25 CenterY=-32.25 CenterZ=0 NormalX=0 NormalY=0 NormalZ=1 AngleXU=0 Radius=1.25
    g1: Circle CenterX=-3.25 CenterY=-32.25 CenterZ=0 NormalX=0 NormalY=0 NormalZ=1 AngleXU=0 Radius=1.25
  constraints (6):
    c: Diameter(g0) = 2.5
    c: Diameter(g1) = 2.5
    c: Distance(g1,g-2) = 3.25
    c: Distance(g0,g-2) = 3.25
    c: DistanceY(g1,g-1) = 32.25
    c: Horizontal(g0,g1)
FEATURE [PartDesign::Pocket] Pocket014
  BaseFeature = -> Pad023
  Direction = (0,0,-1)
  Length = 5
  Length2 = 5
  Placement = pos=(0,0,0) rot=(1,1,1;2.0944rad)
  Profile = -> Sketch053
  ReferenceAxis = -> Sketch053 [N_Axis]
  Refine = true
  Suppressed = false
  Type = 0
FEATURE [Sketcher::SketchObject] Sketch075
  ArcFitTolerance = 1e-06
  AttachmentSupport = -> [Pocket014]
  FullyConstrained = false
  MakeInternals = false
  MapMode = 5
  Placement = pos=(1.4e-14,-1.52e-14,-18) rot=(0,0,-1;1.5708rad)
  sketch-geometry (4):
    g0: LineSegment StartX=8 StartY=1.39844 StartZ=0 EndX=8 EndY=-49.3231 EndZ=0
    g1: LineSegment StartX=8 StartY=-49.3231 StartZ=0 EndX=18 EndY=-49.3231 EndZ=0
    g2: LineSegment StartX=18 StartY=-49.3231 StartZ=0 EndX=18 EndY=1.39844 EndZ=0
    g3: LineSegment StartX=18 StartY=1.39844 StartZ=0 EndX=8 EndY=1.39844 EndZ=0
  constraints (10):
    c: Coincident(g0,g1)
    c: Coincident(g1,g2)
    c: Coincident(g2,g3)
    c: Coincident(g3,g0)
    c: Vertical(g0)
    c: Vertical(g2)
    c: Horizontal(g1)
    c: Horizontal(g3)
    c: Distance(g-2,g2) = 18
    c: Distance(g-2,g0) = 8
FEATURE [PartDesign::Pocket] Pocket029
  BaseFeature = -> Pocket014
  Direction = (0,0,-1)
  Length = 4
  Length2 = 5
  Placement = pos=(0,0,0) rot=(1,1,1;2.0944rad)
  Profile = -> Sketch075
  ReferenceAxis = -> Sketch075 [N_Axis]
  Refine = true
  Suppressed = false
  Type = 0
FEATURE [PartDesign::Body] Body004  label="Bottom"
  AllowCompound = false
  Group = -> [Sketch042,Revolution003,Sketch045,Pocket012,PolarPattern002,Sketch051,Pad022,Sketch052,Pad023,Sketch053,Pocket014,Sketch075,Pocket029]
  Origin = -> Origin010
  Tip = -> Pocket029
COMPONENT P9 — geometry summary ("Nema17"; no construction recipe available for this part):
  bounding box: 49.0 x 48.5 x 42.0 mm
  tessellated surface: 1,764 triangles
  volume: 60608 mm^3 (61% of its bounding box)
COMPONENT P10 — recipe-attached ("SecondNemaHolder001", modeled in this document).
Construction recipe (the document's own serialized feature program — sketch geometry with constraints, then the solid features built on it; lengths are millimeters unless a unit is written):

FEATURE [Sketcher::SketchObject] Sketch076
  ArcFitTolerance = 1e-06
  AttachmentSupport = -> [XY_Plane013]
  FullyConstrained = true
  MakeInternals = false
  MapMode = 5
  sketch-geometry (1):
    g0: Circle CenterX=0 CenterY=0 CenterZ=0 NormalX=0 NormalY=0 NormalZ=1 AngleXU=0 Radius=12.5
  constraints (2):
    c: Diameter(g0) = 25
    c: Coincident(g0,g-1)
FEATURE [PartDesign::Pad] Pad031
  Direction = (0,0,1)
  Length = 10
  Length2 = 10
  Profile = -> Sketch076
  ReferenceAxis = -> Sketch076 [N_Axis]
  Refine = true
  Suppressed = false
  Type = 0
FEATURE [Sketcher::SketchObject] Sketch077
  ArcFitTolerance = 1e-06
  AttachmentSupport = -> [Pad031]
  FullyConstrained = true
  MakeInternals = false
  MapMode = 5
  Placement = pos=(0,0,0) rot=(1,0,0;3.14159rad)
  sketch-geometry (1):
    g0: Circle CenterX=0 CenterY=0 CenterZ=0 NormalX=0 NormalY=0 NormalZ=1 AngleXU=0 Radius=25
  constraints (2):
    c: Diameter(g0) = 50
    c: Coincident(g0,g-1)
FEATURE [PartDesign::Pad] Pad032
  BaseFeature = -> Pad031
  Direction = (0,0,-1)
  Length = 4
  Length2 = 10
  Profile = -> Sketch077
  ReferenceAxis = -> Sketch077 [N_Axis]
  Refine = true
  Suppressed = false
  Type = 0
FEATURE [Sketcher::SketchObject] Sketch078
  ArcFitTolerance = 1e-06
  AttachmentSupport = -> [Pad032]
  FullyConstrained = true
  MakeInternals = false
  MapMode = 5
  sketch-geometry (4):
    g0: ArcOfCircle CenterX=-16.0104 CenterY=16.0104 CenterZ=0 NormalX=0 NormalY=0 NormalZ=1 AngleXU=0 Radius=1.5 StartAngle=0.785398 EndAngle=3.92699
    g1: ArcOfCircle CenterX=-10 CenterY=10 CenterZ=0 NormalX=0 NormalY=0 NormalZ=1 AngleXU=0 Radius=1.5 StartAngle=3.92699 EndAngle=7.06858
    g2: LineSegment StartX=-14.9497 StartY=17.0711 StartZ=0 EndX=-8.93934 EndY=11.0607 EndZ=0
    g3: LineSegment StartX=-17.0711 StartY=14.9497 StartZ=0 EndX=-11.0607 EndY=8.93934 EndZ=0
  constraints (10):
    c: Tangent(g0,g2) = 1.5708
    c: Tangent(g0,g3) = -1.5708
    c: Tangent(g1,g2) = 1.5708
    c: Tangent(g1,g3) = -1.5708
    c: Equal(g0,g1)
    c: Distance(g0,g1) = 8.5
    c: Angle(g-1,g2) = -0.785398
    c: Radius(g0) = 1.5
    c: DistanceX(g1,g-1) = 10
    c: DistanceY(g-1,g1) = 10
FEATURE [PartDesign::Pocket] Pocket030
  BaseFeature = -> Pad032
  Direction = (0,0,-1)
  Length = 5
  Length2 = 5
  Profile = -> Sketch078
  ReferenceAxis = -> Sketch078 [N_Axis]
  Refine = true
  Suppressed = false
  Type = 0
FEATURE [PartDesign::PolarPattern] PolarPattern005
  Angle = 360
  Axis = -> Sketch078 [N_Axis]
  BaseFeature = -> Pocket030
  Mode = 0
  Occurrences = 4
  Offset = 120
  Originals = -> [Pocket030]
  Refine = true
  Suppressed = false
  TransformMode = 0
FEATURE [PartDesign::Body] Body006  label="SecondNemaHolder"
  AllowCompound = false
  Group = -> [Sketch076,Pad031,Sketch077,Pad032,Sketch078,Pocket030,PolarPattern005]
  Origin = -> Origin013
  Placement = pos=(260,0,53) rot=(0,0,1;0rad)
  Tip = -> PolarPattern005
